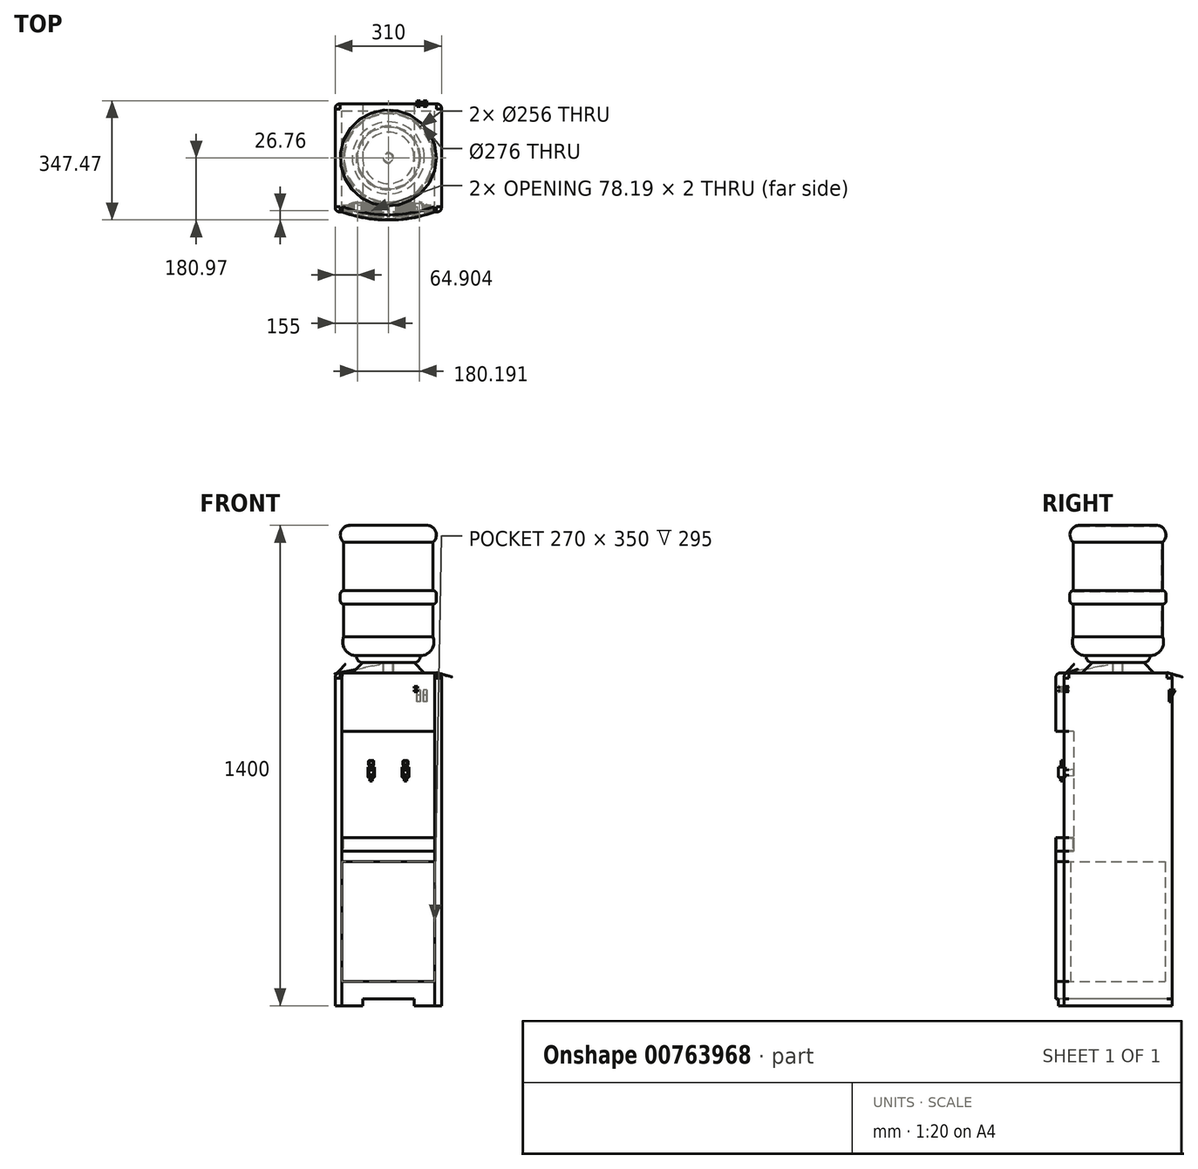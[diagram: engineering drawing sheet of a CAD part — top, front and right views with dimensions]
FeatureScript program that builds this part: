
annotation { "Feature Type Name" : "Feature", "Feature Type Description" : "" }
export const myFeature = defineFeature(function(context is Context, id is Id, definition is map)
    precondition{}
    {
        {
            var Q0;
            Q0=qCreatedBy(makeId("Top.planeOp"),FACE);
            var sketch = newSketch(context, id + "F0", { "sketchPlane" : qUnion([Q0])});
            skLineSegment(sketch, "E0.bottom", {"start": v(155, -157.5) * mm, "end": v(-155, -157.5) * mm});
            skLineSegment(sketch, "E0.top", {"start": v(155, 157.5) * mm, "end": v(-155, 157.5) * mm});
            skLineSegment(sketch, "E0.left", {"start": v(155, -157.5) * mm, "end": v(155, 157.5) * mm});
            skLineSegment(sketch, "E0.right", {"start": v(-155, -157.5) * mm, "end": v(-155, 157.5) * mm});
            skPoint(sketch, "E0.middle", {"position": v(0, 0) * mm});
            skArc(sketch, "E1", {"start": v(-135, -157.5) * mm, "mid": v(0, -180.97) * mm, "end": v(135, -157.5) * mm});
            skSolve(sketch);
        }
        {
            var Q0;
            Q0=makeQuery(id+"F0.imprint","IMPRINT",FACE,{"disambiguationData":[TD([[makeQuery(id+"F0.imprint","IMPRINT",EDGE,{"derivedFrom":sQuery(id+"F0.wireOp",EDGE,"E0.bottom")}),-1.0]])]});
            var Q1;
            {var subQ0=sQuery(id+"F0.wireOp",EDGE,"E1");Q1=makeQuery(id+"F0.imprint","IMPRINT",FACE,{"disambiguationData":[TD([[makeQuery(id+"F0.imprint","IMPRINT",EDGE,{"derivedFrom":subQ0}),1.0]])]});}
            extrude(context, id + "F1", {"entities" : qUnion([Q0, Q1]), "depth" : 970 * mm, "offsetDistance" : 25 * mm});
        }
        {
            var Q0;
            Q0=qCreatedBy(makeId("Front.planeOp"),FACE);
            var sketch = newSketch(context, id + "F2", { "sketchPlane" : qUnion([Q0])});
            skLineSegment(sketch, "E2.0", {"start": v(155, 970) * mm, "end": v(-155, 970) * mm});
            skLineSegment(sketch, "E3", {"start": v(105, 970) * mm, "end": v(75, 1000) * mm});
            skLineSegment(sketch, "E4", {"start": v(75, 1000) * mm, "end": v(0, 1000) * mm});
            skLineSegment(sketch, "E5", {"start": v(0, 1000) * mm, "end": v(0, 970) * mm});
            skLineSegment(sketch, "E6", {"start": v(15, 1000) * mm, "end": v(15, 970) * mm});
            skSolve(sketch);
        }
        {
            var Q0;
            {var subQ0=sQuery(id+"F2.wireOp",EDGE,"E3");Q0=makeQuery(id+"F2.imprint","IMPRINT",FACE,{"disambiguationData":[TD([[makeQuery(id+"F2.imprint","IMPRINT",EDGE,{"derivedFrom":subQ0}),1.0]])]});}
            var Q1;
            Q1=sQuery(id+"F2.wireOp",EDGE,"E5");
            revolve(context, id + "F3", {"operationType" : NewBodyOperationType.ADD, "surfaceOperationType" : NewSurfaceOperationType.NEW, "entities" : qUnion([Q0]), "axis" : qUnion([Q1]), "revolveType" : RevolveType.FULL});
        }
        {
            var Q0;
            Q0=qCreatedBy(makeId("Top.planeOp"),FACE);
            cPlane(context, id + "F4", {"entities" : qUnion([Q0]), "cplaneType" : CPlaneType.OFFSET, "offset" : 450 * mm, "width" : 150 * mm, "height" : 150 * mm});
        }
        {
            var Q0;
            Q0=qCreatedBy(id+"F4.planeOp",FACE);
            var sketch = newSketch(context, id + "F5", { "sketchPlane" : qUnion([Q0])});
            skArc(sketch, "E7.0.0", {"start": v(-135, -157.5) * mm, "mid": v(0, -180.97) * mm, "end": v(135, -157.5) * mm});
            skArc(sketch, "E7.0.2", {"start": v(135, -157.5) * mm, "mid": v(0, -180.97) * mm, "end": v(-135, -157.5) * mm});
            skLineSegment(sketch, "E8", {"start": v(-90, -129.3) * mm, "end": v(0, -129.3) * mm});
            skArc(sketch, "E9", {"start": v(-90, -129.3) * mm, "mid": v(-116.55, -136.93) * mm, "end": v(-135, -157.5) * mm});
            skLineSegment(sketch, "E10.MirrorCS", {"start": v(90, -129.3) * mm, "end": v(0, -129.3) * mm});
            skArc(sketch, "E11.MirrorCS", {"start": v(90, -129.3) * mm, "mid": v(116.55, -136.93) * mm, "end": v(135, -157.5) * mm});
            skSolve(sketch);
        }
        {
            var Q0;
            Q0 = qSketchRegion(id + "F5", true);
            extrude(context, id + "F6", {"entities" : qUnion([Q0]), "operationType" : NewBodyOperationType.REMOVE, "depth" : 350 * mm, "offsetDistance" : 25 * mm});
        }
        {
            var Q0;
            Q0=qCreatedBy(makeId("Front.planeOp"),FACE);
            var sketch = newSketch(context, id + "F7", { "sketchPlane" : qUnion([Q0])});
            skLineSegment(sketch, "E12.0", {"start": v(-135, 450) * mm, "end": v(-135, 0) * mm});
            skLineSegment(sketch, "E12.1", {"start": v(135, 450) * mm, "end": v(135, 0) * mm});
            skLineSegment(sketch, "E13", {"start": v(-135, 420) * mm, "end": v(135, 420) * mm});
            skLineSegment(sketch, "E14", {"start": v(-135, 70) * mm, "end": v(135, 70) * mm});
            skSolve(sketch);
        }
        {
            var Q0;
            Q0 = qSketchRegion(id + "F7", true);
            extrude(context, id + "F8", {"entities" : qUnion([Q0]), "operationType" : NewBodyOperationType.REMOVE, "endBound" : BoundingType.THROUGH_ALL, "depth" : 25 * mm, "offsetDistance" : 25 * mm, "hasSecondDirection" : true, "secondDirectionOppositeDirection" : true, "secondDirectionDepth" : (315 / 2 - 20) * mm});
        }
        {
            var Q0;
            Q0=qCreatedBy(makeId("Front.planeOp"),FACE);
            var sketch = newSketch(context, id + "F9", { "sketchPlane" : qUnion([Q0])});
            skLineSegment(sketch, "E15.bottom", {"start": v(-75, 20) * mm, "end": v(75, 20) * mm});
            skLineSegment(sketch, "E15.top", {"start": v(-75, 0) * mm, "end": v(75, 0) * mm});
            skLineSegment(sketch, "E15.left", {"start": v(-75, 20) * mm, "end": v(-75, 0) * mm});
            skLineSegment(sketch, "E15.right", {"start": v(75, 20) * mm, "end": v(75, 0) * mm});
            skSolve(sketch);
        }
        {
            var Q0;
            Q0 = qSketchRegion(id + "F9", true);
            extrude(context, id + "F10", {"entities" : qUnion([Q0]), "operationType" : NewBodyOperationType.REMOVE, "endBound" : BoundingType.THROUGH_ALL, "oppositeDirection" : true, "depth" : 25 * mm, "offsetDistance" : 25 * mm, "hasSecondDirection" : true, "secondDirectionBound" : SecondDirectionBoundingType.THROUGH_ALL, "secondDirectionOppositeDirection" : false, "secondDirectionDepth" : 25 * mm});
        }
        {
            var Q0;
            Q0=qCreatedBy(makeId("Front.planeOp"),FACE);
            var sketch = newSketch(context, id + "F11", { "sketchPlane" : qUnion([Q0])});
            skLineSegment(sketch, "E16.0", {"start": v(-15, 1000) * mm, "end": v(15, 1000) * mm});
            skLineSegment(sketch, "E17.0.0", {"start": v(-15, 970) * mm, "end": v(15, 970) * mm});
            skLineSegment(sketch, "E18", {"start": v(-15, 970) * mm, "end": v(-15, 1000) * mm});
            skLineSegment(sketch, "E19", {"start": v(0, 1400) * mm, "end": v(-112, 1400) * mm});
            skLineSegment(sketch, "E20", {"start": v(-130, 1350.55) * mm, "end": v(-130, 1210) * mm});
            skLineSegment(sketch, "E21", {"start": v(-130, 1170) * mm, "end": v(-130, 1075) * mm});
            skLineSegment(sketch, "E22.0", {"start": v(-75, 1000) * mm, "end": v(75, 1000) * mm});
            skArc(sketch, "E23", {"start": v(-92.88, 1020.1) * mm, "mid": v(-88.45, 1006.04) * mm, "end": v(-75, 1000) * mm});
            skLineSegment(sketch, "E24", {"start": v(-140, 1200) * mm, "end": v(-140, 1180) * mm});
            skArc(sketch, "E25", {"start": v(-140, 1180) * mm, "mid": v(-137.07, 1172.93) * mm, "end": v(-130, 1170) * mm});
            skLineSegment(sketch, "E26", {"start": v(-140, 1180) * mm, "end": v(-130, 1180) * mm, "construction": true});
            skLineSegment(sketch, "E27", {"start": v(-130, 1170) * mm, "end": v(-130, 1180) * mm, "construction": true});
            skArc(sketch, "E28", {"start": v(-112, 1400) * mm, "mid": v(-138.31, 1381.58) * mm, "end": v(-130, 1350.55) * mm});
            skArc(sketch, "E29", {"start": v(-130, 1210) * mm, "mid": v(-137.07, 1207.07) * mm, "end": v(-140, 1200) * mm});
            skLineSegment(sketch, "E30", {"start": v(-140, 1200) * mm, "end": v(-130, 1200) * mm, "construction": true});
            skLineSegment(sketch, "E31", {"start": v(-130, 1210) * mm, "end": v(-130, 1200) * mm, "construction": true});
            skArc(sketch, "E32", {"start": v(-130, 1075) * mm, "mid": v(-126.01, 1037.7) * mm, "end": v(-92.88, 1020.1) * mm});
            skLineSegment(sketch, "E33", {"start": v(-92.88, 1020.1) * mm, "end": v(0, 1020.1) * mm});
            skLineSegment(sketch, "E34", {"start": v(0, 1400) * mm, "end": v(0, 970) * mm});
            skLineSegment(sketch, "E35.0", {"start": v(-75, 1002) * mm, "end": v(75, 1002) * mm});
            skArc(sketch, "E35.1", {"start": v(-90.44, 1022.18) * mm, "mid": v(-87.7, 1008.28) * mm, "end": v(-75, 1002) * mm});
            skArc(sketch, "E35.2", {"start": v(-128, 1074.6) * mm, "mid": v(-123.77, 1037.98) * mm, "end": v(-90.44, 1022.18) * mm});
            skLineSegment(sketch, "E35.3", {"start": v(-128, 1172.25) * mm, "end": v(-128, 1074.6) * mm});
            skArc(sketch, "E35.4", {"start": v(-138, 1180) * mm, "mid": v(-134.9, 1173.68) * mm, "end": v(-128, 1172.25) * mm});
            skLineSegment(sketch, "E35.5", {"start": v(-138, 1200) * mm, "end": v(-138, 1180) * mm});
            skLineSegment(sketch, "E35.6", {"start": v(0, 1398) * mm, "end": v(-112, 1398) * mm});
            skArc(sketch, "E35.7", {"start": v(-112, 1398) * mm, "mid": v(-136.58, 1380.46) * mm, "end": v(-128, 1351.5) * mm});
            skLineSegment(sketch, "E35.8", {"start": v(-128, 1351.5) * mm, "end": v(-128, 1207.75) * mm});
            skArc(sketch, "E35.9", {"start": v(-128, 1207.75) * mm, "mid": v(-134.9, 1206.32) * mm, "end": v(-138, 1200) * mm});
            skLineSegment(sketch, "E36", {"start": v(-13, 970) * mm, "end": v(-13, 1002) * mm});
            skSolve(sketch);
        }
        {
            var Q0;
            {var subQ0=sQuery(id+"F11.wireOp",EDGE,"E18");Q0=makeQuery(id+"F11.imprint","IMPRINT",FACE,{"disambiguationData":[TD([[makeQuery(id+"F11.imprint","IMPRINT",EDGE,{"derivedFrom":subQ0}),-1.0]])]});}
            var Q1;
            {var subQ1=sQuery(id+"F11.wireOp",EDGE,"E23");Q1=makeQuery(id+"F11.imprint","IMPRINT",FACE,{"disambiguationData":[TD([[makeQuery(id+"F11.imprint","IMPRINT",EDGE,{"derivedFrom":subQ1}),1.0]])]});}
            var Q2;
            {var subQ1=sQuery(id+"F11.wireOp",EDGE,"E19");Q2=makeQuery(id+"F11.imprint","IMPRINT",FACE,{"disambiguationData":[TD([[makeQuery(id+"F11.imprint","IMPRINT",EDGE,{"derivedFrom":subQ1}),1.0]])]});}
            var Q3;
            Q3=sQuery(id+"F11.wireOp",EDGE,"E34");
            revolve(context, id + "F12", {"surfaceOperationType" : NewSurfaceOperationType.NEW, "entities" : qUnion([Q0, Q1, Q2]), "axis" : qUnion([Q3]), "revolveType" : RevolveType.FULL});
        }
        {
            var Q0;
            Q0=makeQuery(id+"F1.opExtrude","SWEPT_EDGE",EDGE,{"disambiguationData":[OSD([sQuery(id+"F0.wireOp",EDGE,"E0.top"),sQuery(id+"F0.wireOp",EDGE,"E0.right")])]});
            var Q1;
            Q1=makeQuery(id+"F1.opExtrude","SWEPT_EDGE",EDGE,{"disambiguationData":[OSD([sQuery(id+"F0.wireOp",EDGE,"E0.bottom"),sQuery(id+"F0.wireOp",EDGE,"E0.right")])]});
            var Q2;
            Q2=makeQuery(id+"F1.opExtrude","SWEPT_EDGE",EDGE,{"disambiguationData":[OSD([sQuery(id+"F0.wireOp",EDGE,"E0.bottom"),sQuery(id+"F0.wireOp",EDGE,"E0.left")])]});
            var Q3;
            Q3=makeQuery(id+"F1.opExtrude","SWEPT_EDGE",EDGE,{"disambiguationData":[OSD([sQuery(id+"F0.wireOp",EDGE,"E0.top"),sQuery(id+"F0.wireOp",EDGE,"E0.left")])]});
            var Q4;
            Q4=makeQuery(id+"F1.opExtrude","CAP_EDGE",EDGE,{"disambiguationData":[OSD([sQuery(id+"F0.wireOp",EDGE,"E0.top")])],"isStart":false});
            var Q5;
            Q5=makeQuery(id+"F1.opExtrude","CAP_EDGE",EDGE,{"disambiguationData":[OSD([sQuery(id+"F0.wireOp",EDGE,"E0.left")])],"isStart":false});
            var Q6;
            Q6=makeQuery(id+"F1.opExtrude","CAP_EDGE",EDGE,{"disambiguationData":[OSD([sQuery(id+"F0.wireOp",EDGE,"E0.right")])],"isStart":false});
            var Q7;
            Q7=makeQuery(id+"F1.opExtrude","CAP_EDGE",EDGE,{"disambiguationData":[OSD([sQuery(id+"F0.wireOp",EDGE,"E1")])],"isStart":false});
            var Q8;
            {var subQ0=sQuery(id+"F0.wireOp",EDGE,"E0.bottom");Q8=makeQuery(id+"F1.opExtrude","CAP_EDGE",EDGE,{"disambiguationData":[OSD([subQ0]),TDD([makeQuery(id+"F0.imprint","IMPRINT",EDGE,{"disambiguationData":[TD([[makeQuery(id+"F0.imprint","INTERSECT",VERTEX,{"derivedFrom":[subQ0,sQuery(id+"F0.wireOp",EDGE,"E0.right")]}),1.0]])],"derivedFrom":subQ0})])],"isStart":false});}
            var Q9;
            {var subQ0=sQuery(id+"F0.wireOp",EDGE,"E0.bottom");Q9=makeQuery(id+"F1.opExtrude","CAP_EDGE",EDGE,{"disambiguationData":[OSD([subQ0]),TDD([makeQuery(id+"F0.imprint","IMPRINT",EDGE,{"disambiguationData":[TD([[makeQuery(id+"F0.imprint","INTERSECT",VERTEX,{"derivedFrom":[subQ0,sQuery(id+"F0.wireOp",EDGE,"E0.left")]}),-1.0]])],"derivedFrom":subQ0})])],"isStart":false});}
            fillet(context, id + "F13", {"entities" : qUnion([Q0, Q1, Q2, Q3, Q4, Q5, Q6, Q7, Q8, Q9]), "radius" : 15 * mm, "tangentPropagation" : true, "crossSection" : FilletCrossSection.CURVATURE, "magnitude" : 0.5, "defaultsChanged" : false, "vertexSettings" : []});
        }
        {
            var Q0;
            Q0=makeQuery(id+"F6.boolean.opBoolean","COPY",FACE,{"derivedFrom":makeQuery(id+"F6.opExtrude","CAP_FACE",FACE,{"disambiguationData":[OSD([sQuery(id+"F5.wireOp",EDGE,"E7.0.2"),sQuery(id+"F5.wireOp",EDGE,"E8"),sQuery(id+"F5.wireOp",EDGE,"E9"),sQuery(id+"F5.wireOp",EDGE,"E10.MirrorCS"),sQuery(id+"F5.wireOp",EDGE,"E11.MirrorCS")])],"isStart":true})});
            var sketch = newSketch(context, id + "F14", { "sketchPlane" : qUnion([Q0])});
            skArc(sketch, "E37.0", {"start": v(-90, -129.3) * mm, "mid": v(-116.55, -136.93) * mm, "end": v(-135, -157.5) * mm});
            skLineSegment(sketch, "E37.1", {"start": v(90, -129.3) * mm, "end": v(-90, -129.3) * mm});
            skArc(sketch, "E37.2", {"start": v(90, -129.3) * mm, "mid": v(116.55, -136.93) * mm, "end": v(135, -157.5) * mm});
            skArc(sketch, "E37.3", {"start": v(135, -157.5) * mm, "mid": v(0, -180.97) * mm, "end": v(-135, -157.5) * mm});
            skSolve(sketch);
        }
        {
            var Q0;
            Q0=makeQuery(id+"F14.imprint","IMPRINT",FACE,{"disambiguationData":[TD([[makeQuery(id+"F14.imprint","IMPRINT",EDGE,{"derivedFrom":sQuery(id+"F14.wireOp",EDGE,"E37.0")}),1.0]])]});
            var Q1;
            Q1 = qConstructionFilter(qBodyType(qCreatedBy(id + "F14" ,EDGE), BodyType.WIRE), ConstructionObject.NO);
            extrude(context, id + "F15", {"entities" : qUnion([Q0]), "surfaceEntities" : qUnion([Q1]), "depth" : 40 * mm, "offsetDistance" : 25 * mm});
        }
        {
            var Q0;
            Q0=makeQuery(id+"F15.opExtrude","CAP_FACE",FACE,{"disambiguationData":[OSD([sQuery(id+"F14.wireOp",EDGE,"E37.0"),sQuery(id+"F14.wireOp",EDGE,"E37.1"),sQuery(id+"F14.wireOp",EDGE,"E37.2"),sQuery(id+"F14.wireOp",EDGE,"E37.3")])],"isStart":false});
            shell(context, id + "F16", {"entities" : qUnion([Q0]), "thickness" : 2 * mm});
        }
        {
            var Q0;
            Q0=makeQuery(id+"F15.opExtrude","CAP_FACE",FACE,{"disambiguationData":[OSD([sQuery(id+"F14.wireOp",EDGE,"E37.0"),sQuery(id+"F14.wireOp",EDGE,"E37.1"),sQuery(id+"F14.wireOp",EDGE,"E37.2"),sQuery(id+"F14.wireOp",EDGE,"E37.3")])],"isStart":false});
            var sketch = newSketch(context, id + "F17", { "sketchPlane" : qUnion([Q0])});
            skArc(sketch, "E38.0", {"start": v(-90, -131.3) * mm, "mid": v(-114.54, -138.04) * mm, "end": v(-132.18, -156.38) * mm});
            skLineSegment(sketch, "E38.1", {"start": v(90, -131.3) * mm, "end": v(-90, -131.3) * mm});
            skArc(sketch, "E38.2", {"start": v(132.18, -156.38) * mm, "mid": v(0, -178.97) * mm, "end": v(-132.18, -156.38) * mm});
            skArc(sketch, "E38.3", {"start": v(90, -131.3) * mm, "mid": v(114.54, -138.04) * mm, "end": v(132.18, -156.38) * mm});
            skLineSegment(sketch, "E39.0", {"start": v(90, -133.3) * mm, "end": v(-90, -133.3) * mm});
            skArc(sketch, "E39.1", {"start": v(90, -133.3) * mm, "mid": v(112.5, -139.17) * mm, "end": v(129.24, -155.29) * mm});
            skArc(sketch, "E39.2", {"start": v(129.24, -155.29) * mm, "mid": v(0, -176.97) * mm, "end": v(-129.24, -155.29) * mm});
            skArc(sketch, "E39.3", {"start": v(-90, -133.3) * mm, "mid": v(-112.5, -139.17) * mm, "end": v(-129.24, -155.29) * mm});
            skLineSegment(sketch, "E40", {"start": v(0, -112.71) * mm, "end": v(0, -215.15) * mm, "construction": true});
            skLineSegment(sketch, "E41", {"start": v(-50, -106.6) * mm, "end": v(-50, -205.9) * mm, "construction": true});
            skLineSegment(sketch, "E42.bottom", {"start": v(-57.5, -156.3) * mm, "end": v(-42.5, -156.3) * mm});
            skLineSegment(sketch, "E42.top", {"start": v(-57.5, -171.3) * mm, "end": v(-42.5, -171.3) * mm});
            skLineSegment(sketch, "E42.left", {"start": v(-57.5, -156.3) * mm, "end": v(-57.5, -171.3) * mm});
            skLineSegment(sketch, "E42.right", {"start": v(-42.5, -156.3) * mm, "end": v(-42.5, -171.3) * mm});
            skLineSegment(sketch, "E43", {"start": v(-51, -156.3) * mm, "end": v(-51, -133.3) * mm});
            skLineSegment(sketch, "E44.MirrorCS", {"start": v(-49, -156.3) * mm, "end": v(-49, -133.3) * mm});
            skLineSegment(sketch, "E45", {"start": v(-51, -171.3) * mm, "end": v(-51, -173.67) * mm});
            skLineSegment(sketch, "E46", {"start": v(-49, -171.3) * mm, "end": v(-49, -173.93) * mm});
            skLineSegment(sketch, "E47", {"start": v(-1, -133.3) * mm, "end": v(-1, -176.97) * mm});
            skLineSegment(sketch, "E48", {"start": v(1, -133.3) * mm, "end": v(1, -176.97) * mm});
            skLineSegment(sketch, "E49", {"start": v(-49, -135.21) * mm, "end": v(-1, -135.21) * mm});
            skLineSegment(sketch, "E50.0.1.0", {"start": v(-49, -137.21) * mm, "end": v(-1, -137.21) * mm});
            skLineSegment(sketch, "E50.0.2.0", {"start": v(-49, -139.21) * mm, "end": v(-1, -139.21) * mm});
            skLineSegment(sketch, "E50.0.3.0", {"start": v(-49, -141.21) * mm, "end": v(-1, -141.21) * mm});
            skLineSegment(sketch, "E50.0.4.0", {"start": v(-49, -143.21) * mm, "end": v(-1, -143.21) * mm});
            skLineSegment(sketch, "E50.0.5.0", {"start": v(-49, -145.21) * mm, "end": v(-1, -145.21) * mm});
            skLineSegment(sketch, "E50.0.6.0", {"start": v(-49, -147.21) * mm, "end": v(-1, -147.21) * mm});
            skLineSegment(sketch, "E50.0.7.0", {"start": v(-49, -149.21) * mm, "end": v(-1, -149.21) * mm});
            skLineSegment(sketch, "E50.0.8.0", {"start": v(-49, -151.21) * mm, "end": v(-1, -151.21) * mm});
            skLineSegment(sketch, "E50.0.9.0", {"start": v(-49, -153.21) * mm, "end": v(-1, -153.21) * mm});
            skLineSegment(sketch, "E50.0.10.0", {"start": v(-49, -155.21) * mm, "end": v(-1, -155.21) * mm});
            skLineSegment(sketch, "E50.0.11.0", {"start": v(-42.5, -157.21) * mm, "end": v(-1, -157.21) * mm});
            skLineSegment(sketch, "E50.0.12.0", {"start": v(-44.5, -159.21) * mm, "end": v(-1, -159.21) * mm});
            skLineSegment(sketch, "E50.0.13.0", {"start": v(-44.5, -161.21) * mm, "end": v(-1, -161.21) * mm});
            skLineSegment(sketch, "E50.0.14.0", {"start": v(-44.5, -163.21) * mm, "end": v(-1, -163.21) * mm});
            skLineSegment(sketch, "E50.0.15.0", {"start": v(-49, -165.21) * mm, "end": v(-1, -165.21) * mm});
            skLineSegment(sketch, "E50.0.16.0", {"start": v(-49, -167.21) * mm, "end": v(-1, -167.21) * mm});
            skLineSegment(sketch, "E50.0.17.0", {"start": v(-49, -169.21) * mm, "end": v(-1, -169.21) * mm});
            skLineSegment(sketch, "E50.0.18.0", {"start": v(-49, -171.21) * mm, "end": v(-1, -171.21) * mm});
            skLineSegment(sketch, "E50.0.19.0", {"start": v(-49, -173.21) * mm, "end": v(-1, -173.21) * mm});
            skLineSegment(sketch, "E50.0.20.0", {"start": v(-49, -175.21) * mm, "end": v(-1, -175.21) * mm});
            skLineSegment(sketch, "E50.direction1", {"start": v(-49, -135.21) * mm, "end": v(-24, -135.21) * mm, "construction": true});
            skLineSegment(sketch, "E50.direction2", {"start": v(-49, -135.21) * mm, "end": v(-49, -137.21) * mm, "construction": true});
            skLineSegment(sketch, "E51.MirrorCS", {"start": v(-51, -137.21) * mm, "end": v(-108.57, -137.21) * mm});
            skLineSegment(sketch, "E52.MirrorCS", {"start": v(-51, -139.21) * mm, "end": v(-112.57, -139.21) * mm});
            skLineSegment(sketch, "E53.MirrorCS", {"start": v(-51, -141.21) * mm, "end": v(-115.8, -141.21) * mm});
            skLineSegment(sketch, "E54.MirrorCS", {"start": v(-51, -143.21) * mm, "end": v(-118.53, -143.21) * mm});
            skLineSegment(sketch, "E55.MirrorCS", {"start": v(-51, -145.21) * mm, "end": v(-120.9, -145.21) * mm});
            skLineSegment(sketch, "E56.MirrorCS", {"start": v(-51, -147.21) * mm, "end": v(-122.96, -147.21) * mm});
            skLineSegment(sketch, "E57.MirrorCS", {"start": v(-51, -149.21) * mm, "end": v(-124.8, -149.21) * mm});
            skLineSegment(sketch, "E58.MirrorCS", {"start": v(-51, -151.21) * mm, "end": v(-126.43, -151.21) * mm});
            skLineSegment(sketch, "E59.MirrorCS", {"start": v(-51, -153.21) * mm, "end": v(-127.89, -153.21) * mm});
            skLineSegment(sketch, "E60.MirrorCS", {"start": v(-51, -155.21) * mm, "end": v(-129.2, -155.21) * mm});
            skLineSegment(sketch, "E61.MirrorCS", {"start": v(-57.5, -157.21) * mm, "end": v(-123.53, -157.21) * mm});
            skLineSegment(sketch, "E62.MirrorCS", {"start": v(-57.5, -159.21) * mm, "end": v(-117.26, -159.21) * mm});
            skLineSegment(sketch, "E63.MirrorCS", {"start": v(-57.5, -161.21) * mm, "end": v(-110.6, -161.21) * mm});
            skLineSegment(sketch, "E64.MirrorCS", {"start": v(-57.5, -163.21) * mm, "end": v(-103.48, -163.21) * mm});
            skLineSegment(sketch, "E65.MirrorCS", {"start": v(-49, -165.21) * mm, "end": v(-50, -165.21) * mm});
            skLineSegment(sketch, "E66.MirrorCS", {"start": v(-57.5, -167.21) * mm, "end": v(-99, -167.21) * mm});
            skLineSegment(sketch, "E67.MirrorCS", {"start": v(-57.5, -169.21) * mm, "end": v(-99, -169.21) * mm});
            skLineSegment(sketch, "E68.MirrorCS", {"start": v(-51, -171.21) * mm, "end": v(-99, -171.21) * mm});
            skLineSegment(sketch, "E69.MirrorCS", {"start": v(-51, -173.21) * mm, "end": v(-99, -173.21) * mm});
            skPoint(sketch, "E70.orphan", {"position": v(-99, -137.21) * mm});
            skPoint(sketch, "E71.orphan", {"position": v(-99, -139.21) * mm});
            skPoint(sketch, "E72.orphan", {"position": v(-99, -141.21) * mm});
            skPoint(sketch, "E73.orphan", {"position": v(-99, -143.21) * mm});
            skPoint(sketch, "E74.orphan", {"position": v(-99, -145.21) * mm});
            skPoint(sketch, "E75.orphan", {"position": v(-99, -147.21) * mm});
            skPoint(sketch, "E76.orphan", {"position": v(-99, -149.21) * mm});
            skPoint(sketch, "E77.orphan", {"position": v(-99, -151.21) * mm});
            skPoint(sketch, "E78.orphan", {"position": v(-99, -153.21) * mm});
            skPoint(sketch, "E79.orphan", {"position": v(-99, -155.21) * mm});
            skPoint(sketch, "E80.orphan", {"position": v(-99, -157.21) * mm});
            skPoint(sketch, "E81.orphan", {"position": v(-99, -159.21) * mm});
            skPoint(sketch, "E82.orphan", {"position": v(-99, -161.21) * mm});
            skPoint(sketch, "E83.orphan", {"position": v(-99, -163.21) * mm});
            skLineSegment(sketch, "E84", {"start": v(-51, -135.21) * mm, "end": v(-103.14, -135.21) * mm});
            skLineSegment(sketch, "E85.0", {"start": v(-55.5, -158.3) * mm, "end": v(-44.5, -158.3) * mm});
            skLineSegment(sketch, "E85.1", {"start": v(-55.5, -158.3) * mm, "end": v(-55.5, -169.3) * mm});
            skLineSegment(sketch, "E85.2", {"start": v(-55.5, -169.3) * mm, "end": v(-44.5, -169.3) * mm});
            skLineSegment(sketch, "E85.3", {"start": v(-44.5, -158.3) * mm, "end": v(-44.5, -169.3) * mm});
            skPoint(sketch, "E86.orphan", {"position": v(-51, -157.21) * mm});
            skPoint(sketch, "E87.orphan", {"position": v(-51, -161.21) * mm});
            skPoint(sketch, "E88.orphan", {"position": v(-51, -165.21) * mm});
            skPoint(sketch, "E89.orphan", {"position": v(-51, -159.21) * mm});
            skPoint(sketch, "E90.orphan", {"position": v(-51, -163.21) * mm});
            skLineSegment(sketch, "E91.trimOffspring", {"start": v(-57.5, -165.21) * mm, "end": v(-99, -165.21) * mm});
            skPoint(sketch, "E92.orphan", {"position": v(-51, -167.21) * mm});
            skPoint(sketch, "E93.orphan", {"position": v(-51, -169.21) * mm});
            skPoint(sketch, "E94.orphan", {"position": v(-49, -159.21) * mm});
            skPoint(sketch, "E95.orphan", {"position": v(-49, -157.21) * mm});
            skPoint(sketch, "E96.orphan", {"position": v(-49, -161.21) * mm});
            skPoint(sketch, "E97.orphan", {"position": v(-49, -163.21) * mm});
            skLineSegment(sketch, "E98.MirrorCS", {"start": v(49, -165.21) * mm, "end": v(1, -165.21) * mm});
            skLineSegment(sketch, "E99.MirrorCS", {"start": v(44.5, -163.21) * mm, "end": v(1, -163.21) * mm});
            skLineSegment(sketch, "E100.MirrorCS", {"start": v(49, -167.21) * mm, "end": v(1, -167.21) * mm});
            skLineSegment(sketch, "E101.MirrorCS", {"start": v(44.5, -159.21) * mm, "end": v(1, -159.21) * mm});
            skLineSegment(sketch, "E102.MirrorCS", {"start": v(49, -171.21) * mm, "end": v(1, -171.21) * mm});
            skLineSegment(sketch, "E103.MirrorCS", {"start": v(42.5, -157.21) * mm, "end": v(1, -157.21) * mm});
            skLineSegment(sketch, "E104.MirrorCS", {"start": v(49, -175.21) * mm, "end": v(1, -175.21) * mm});
            skLineSegment(sketch, "E105.MirrorCS", {"start": v(49, -173.21) * mm, "end": v(1, -173.21) * mm});
            skLineSegment(sketch, "E106.MirrorCS", {"start": v(44.5, -161.21) * mm, "end": v(1, -161.21) * mm});
            skLineSegment(sketch, "E107.MirrorCS", {"start": v(49, -169.21) * mm, "end": v(1, -169.21) * mm});
            skLineSegment(sketch, "E108.MirrorCS", {"start": v(49, -135.21) * mm, "end": v(1, -135.21) * mm});
            skLineSegment(sketch, "E109.MirrorCS", {"start": v(49, -145.21) * mm, "end": v(1, -145.21) * mm});
            skLineSegment(sketch, "E110.MirrorCS", {"start": v(49, -137.21) * mm, "end": v(1, -137.21) * mm});
            skLineSegment(sketch, "E111.MirrorCS", {"start": v(49, -143.21) * mm, "end": v(1, -143.21) * mm});
            skLineSegment(sketch, "E112.MirrorCS", {"start": v(49, -153.21) * mm, "end": v(1, -153.21) * mm});
            skLineSegment(sketch, "E113.MirrorCS", {"start": v(49, -141.21) * mm, "end": v(1, -141.21) * mm});
            skLineSegment(sketch, "E114.MirrorCS", {"start": v(49, -151.21) * mm, "end": v(1, -151.21) * mm});
            skLineSegment(sketch, "E115.MirrorCS", {"start": v(49, -149.21) * mm, "end": v(1, -149.21) * mm});
            skLineSegment(sketch, "E116.MirrorCS", {"start": v(49, -147.21) * mm, "end": v(1, -147.21) * mm});
            skLineSegment(sketch, "E117.MirrorCS", {"start": v(49, -139.21) * mm, "end": v(1, -139.21) * mm});
            skLineSegment(sketch, "E118.MirrorCS", {"start": v(49, -155.21) * mm, "end": v(1, -155.21) * mm});
            skLineSegment(sketch, "E119.MirrorCS", {"start": v(42.5, -156.3) * mm, "end": v(42.5, -171.3) * mm});
            skLineSegment(sketch, "E120.MirrorCS", {"start": v(44.5, -158.3) * mm, "end": v(44.5, -169.3) * mm});
            skLineSegment(sketch, "E121.MirrorCS", {"start": v(55.5, -158.3) * mm, "end": v(55.5, -169.3) * mm});
            skLineSegment(sketch, "E122.MirrorCS", {"start": v(57.5, -156.3) * mm, "end": v(42.5, -156.3) * mm});
            skLineSegment(sketch, "E123.MirrorCS", {"start": v(51, -171.21) * mm, "end": v(99, -171.21) * mm});
            skLineSegment(sketch, "E124.MirrorCS", {"start": v(57.5, -156.3) * mm, "end": v(57.5, -171.3) * mm});
            skLineSegment(sketch, "E125.MirrorCS", {"start": v(57.5, -171.3) * mm, "end": v(42.5, -171.3) * mm});
            skLineSegment(sketch, "E126.MirrorCS", {"start": v(49, -171.3) * mm, "end": v(49, -173.93) * mm});
            skLineSegment(sketch, "E127.MirrorCS", {"start": v(51, -171.3) * mm, "end": v(51, -173.67) * mm});
            skLineSegment(sketch, "E128.MirrorCS", {"start": v(51, -151.21) * mm, "end": v(126.43, -151.21) * mm});
            skLineSegment(sketch, "E129.MirrorCS", {"start": v(51, -155.21) * mm, "end": v(129.2, -155.21) * mm});
            skLineSegment(sketch, "E130.MirrorCS", {"start": v(57.5, -165.21) * mm, "end": v(99, -165.21) * mm});
            skLineSegment(sketch, "E131.MirrorCS", {"start": v(57.5, -157.21) * mm, "end": v(123.53, -157.21) * mm});
            skLineSegment(sketch, "E132.MirrorCS", {"start": v(51, -153.21) * mm, "end": v(127.89, -153.21) * mm});
            skLineSegment(sketch, "E133.MirrorCS", {"start": v(57.5, -159.21) * mm, "end": v(117.26, -159.21) * mm});
            skLineSegment(sketch, "E134.MirrorCS", {"start": v(57.5, -167.21) * mm, "end": v(99, -167.21) * mm});
            skLineSegment(sketch, "E135.MirrorCS", {"start": v(51, -141.21) * mm, "end": v(115.8, -141.21) * mm});
            skLineSegment(sketch, "E136.MirrorCS", {"start": v(51, -149.21) * mm, "end": v(124.8, -149.21) * mm});
            skLineSegment(sketch, "E137.MirrorCS", {"start": v(51, -147.21) * mm, "end": v(122.96, -147.21) * mm});
            skLineSegment(sketch, "E138.MirrorCS", {"start": v(51, -137.21) * mm, "end": v(108.57, -137.21) * mm});
            skLineSegment(sketch, "E139.MirrorCS", {"start": v(57.5, -169.21) * mm, "end": v(99, -169.21) * mm});
            skLineSegment(sketch, "E140.MirrorCS", {"start": v(51, -145.21) * mm, "end": v(120.9, -145.21) * mm});
            skLineSegment(sketch, "E141.MirrorCS", {"start": v(51, -139.21) * mm, "end": v(112.57, -139.21) * mm});
            skLineSegment(sketch, "E142.MirrorCS", {"start": v(51, -135.21) * mm, "end": v(103.14, -135.21) * mm});
            skLineSegment(sketch, "E143.MirrorCS", {"start": v(-90, -133.3) * mm, "end": v(90, -133.3) * mm});
            skLineSegment(sketch, "E144.MirrorCS", {"start": v(51, -143.21) * mm, "end": v(118.53, -143.21) * mm});
            skLineSegment(sketch, "E145.MirrorCS", {"start": v(57.5, -163.21) * mm, "end": v(103.48, -163.21) * mm});
            skLineSegment(sketch, "E146.MirrorCS", {"start": v(57.5, -161.21) * mm, "end": v(110.6, -161.21) * mm});
            skPoint(sketch, "E147.MirrorP", {"position": v(99, -145.21) * mm});
            skPoint(sketch, "E148.MirrorP", {"position": v(99, -141.21) * mm});
            skPoint(sketch, "E149.MirrorP", {"position": v(99, -143.21) * mm});
            skPoint(sketch, "E150.MirrorP", {"position": v(99, -139.21) * mm});
            skPoint(sketch, "E151.MirrorP", {"position": v(99, -137.21) * mm});
            skPoint(sketch, "E152.MirrorP", {"position": v(99, -155.21) * mm});
            skPoint(sketch, "E153.MirrorP", {"position": v(99, -147.21) * mm});
            skPoint(sketch, "E154.MirrorP", {"position": v(99, -149.21) * mm});
            skPoint(sketch, "E155.MirrorP", {"position": v(99, -157.21) * mm});
            skPoint(sketch, "E156.MirrorP", {"position": v(99, -151.21) * mm});
            skPoint(sketch, "E157.MirrorP", {"position": v(99, -153.21) * mm});
            skLineSegment(sketch, "E158.MirrorCS", {"start": v(55.5, -158.3) * mm, "end": v(44.5, -158.3) * mm});
            skLineSegment(sketch, "E159.MirrorCS", {"start": v(55.5, -169.3) * mm, "end": v(44.5, -169.3) * mm});
            skLineSegment(sketch, "E160.MirrorCS", {"start": v(51, -156.3) * mm, "end": v(51, -133.3) * mm});
            skLineSegment(sketch, "E161.MirrorCS", {"start": v(49, -156.3) * mm, "end": v(49, -133.3) * mm});
            skLineSegment(sketch, "E162.MirrorCS", {"start": v(51, -173.21) * mm, "end": v(99, -173.21) * mm});
            skSolve(sketch);
        }
        {
            var Q0;
            {var subQ16=sQuery(id+"F17.wireOp",EDGE,"E38.0");Q0=makeQuery(id+"F17.imprint","IMPRINT",FACE,{"disambiguationData":[TD([[makeQuery(id+"F17.imprint","IMPRINT",EDGE,{"derivedFrom":subQ16}),1.0]])]});}
            var Q1;
            {var subQ0=sQuery(id+"F17.wireOp",EDGE,"E66.MirrorCS");var subQ1=sQuery(id+"F17.wireOp",EDGE,"E38.2");var subQ2=makeQuery(id+"F17.imprint","INTERSECT",VERTEX,{"derivedFrom":[subQ1,subQ0]});Q1=makeQuery(id+"F17.imprint","IMPRINT",FACE,{"disambiguationData":[TD([[makeQuery(id+"F17.imprint","IMPRINT",EDGE,{"disambiguationData":[TD([[subQ2,1.0]])],"derivedFrom":subQ1}),-1.0]])]});}
            var Q2;
            {var subQ0=sQuery(id+"F17.wireOp",EDGE,"E67.MirrorCS");var subQ1=sQuery(id+"F17.wireOp",EDGE,"E38.2");var subQ2=makeQuery(id+"F17.imprint","INTERSECT",VERTEX,{"derivedFrom":[subQ1,subQ0]});Q2=makeQuery(id+"F17.imprint","IMPRINT",FACE,{"disambiguationData":[TD([[makeQuery(id+"F17.imprint","IMPRINT",EDGE,{"disambiguationData":[TD([[subQ2,1.0]])],"derivedFrom":subQ1}),-1.0]])]});}
            var Q3;
            {var subQ0=sQuery(id+"F17.wireOp",EDGE,"E68.MirrorCS");var subQ1=sQuery(id+"F17.wireOp",EDGE,"E38.2");var subQ2=makeQuery(id+"F17.imprint","INTERSECT",VERTEX,{"derivedFrom":[subQ1,subQ0]});Q3=makeQuery(id+"F17.imprint","IMPRINT",FACE,{"disambiguationData":[TD([[makeQuery(id+"F17.imprint","IMPRINT",EDGE,{"disambiguationData":[TD([[subQ2,1.0]])],"derivedFrom":subQ1}),-1.0]])]});}
            var Q4;
            {var subQ0=sQuery(id+"F17.wireOp",EDGE,"E134.MirrorCS");var subQ1=sQuery(id+"F17.wireOp",EDGE,"E38.2");var subQ2=makeQuery(id+"F17.imprint","INTERSECT",VERTEX,{"derivedFrom":[subQ1,subQ0]});Q4=makeQuery(id+"F17.imprint","IMPRINT",FACE,{"disambiguationData":[TD([[makeQuery(id+"F17.imprint","IMPRINT",EDGE,{"disambiguationData":[TD([[subQ2,-1.0]])],"derivedFrom":subQ1}),-1.0]])]});}
            var Q5;
            {var subQ0=sQuery(id+"F17.wireOp",EDGE,"E123.MirrorCS");var subQ1=sQuery(id+"F17.wireOp",EDGE,"E38.2");var subQ2=makeQuery(id+"F17.imprint","INTERSECT",VERTEX,{"derivedFrom":[subQ1,subQ0]});Q5=makeQuery(id+"F17.imprint","IMPRINT",FACE,{"disambiguationData":[TD([[makeQuery(id+"F17.imprint","IMPRINT",EDGE,{"disambiguationData":[TD([[subQ2,1.0]])],"derivedFrom":subQ1}),-1.0]])]});}
            var Q6;
            {var subQ7=sQuery(id+"F17.wireOp",EDGE,"E69.MirrorCS");var subQ9=sQuery(id+"F17.wireOp",EDGE,"E38.2");var subQ10=makeQuery(id+"F17.imprint","INTERSECT",VERTEX,{"derivedFrom":[subQ9,subQ7]});Q6=makeQuery(id+"F17.imprint","IMPRINT",FACE,{"disambiguationData":[TD([[makeQuery(id+"F17.imprint","IMPRINT",EDGE,{"disambiguationData":[TD([[subQ10,1.0]])],"derivedFrom":subQ9}),-1.0]])]});}
            var Q7;
            {var subQ0=sQuery(id+"F17.wireOp",EDGE,"E162.MirrorCS");var subQ1=sQuery(id+"F17.wireOp",EDGE,"E38.2");var subQ2=makeQuery(id+"F17.imprint","INTERSECT",VERTEX,{"derivedFrom":[subQ1,subQ0]});Q7=makeQuery(id+"F17.imprint","IMPRINT",FACE,{"disambiguationData":[TD([[makeQuery(id+"F17.imprint","IMPRINT",EDGE,{"disambiguationData":[TD([[subQ2,1.0]])],"derivedFrom":subQ1}),-1.0]])]});}
            extrude(context, id + "F18", {"entities" : qUnion([Q0, Q1, Q2, Q3, Q4, Q5, Q6, Q7]), "oppositeDirection" : true, "depth" : 2 * mm, "offsetDistance" : 25 * mm});
        }
        {
            var Q0;
            {var subQ0=sQuery(id+"F17.wireOp",EDGE,"E47");var subQ7=sQuery(id+"F17.wireOp",EDGE,"E39.2");var subQ8=makeQuery(id+"F17.imprint","INTERSECT",VERTEX,{"derivedFrom":[subQ7,subQ0]});Q0=makeQuery(id+"F17.imprint","IMPRINT",FACE,{"disambiguationData":[TD([[makeQuery(id+"F17.imprint","IMPRINT",EDGE,{"disambiguationData":[TD([[subQ8,1.0]])],"derivedFrom":subQ7}),-1.0]])]});}
            var Q1;
            {var subQ0=sQuery(id+"F17.wireOp",EDGE,"E49");Q1=makeQuery(id+"F17.imprint","IMPRINT",FACE,{"disambiguationData":[TD([[makeQuery(id+"F17.imprint","IMPRINT",EDGE,{"derivedFrom":subQ0}),-1.0]])]});}
            var Q2;
            {var subQ0=sQuery(id+"F17.wireOp",EDGE,"E50.0.2.0");Q2=makeQuery(id+"F17.imprint","IMPRINT",FACE,{"disambiguationData":[TD([[makeQuery(id+"F17.imprint","IMPRINT",EDGE,{"derivedFrom":subQ0}),-1.0]])]});}
            var Q3;
            {var subQ0=sQuery(id+"F17.wireOp",EDGE,"E50.0.4.0");Q3=makeQuery(id+"F17.imprint","IMPRINT",FACE,{"disambiguationData":[TD([[makeQuery(id+"F17.imprint","IMPRINT",EDGE,{"derivedFrom":subQ0}),-1.0]])]});}
            var Q4;
            {var subQ0=sQuery(id+"F17.wireOp",EDGE,"E50.0.6.0");Q4=makeQuery(id+"F17.imprint","IMPRINT",FACE,{"disambiguationData":[TD([[makeQuery(id+"F17.imprint","IMPRINT",EDGE,{"derivedFrom":subQ0}),-1.0]])]});}
            var Q5;
            {var subQ0=sQuery(id+"F17.wireOp",EDGE,"E50.0.8.0");Q5=makeQuery(id+"F17.imprint","IMPRINT",FACE,{"disambiguationData":[TD([[makeQuery(id+"F17.imprint","IMPRINT",EDGE,{"derivedFrom":subQ0}),-1.0]])]});}
            var Q6;
            {var subQ0=sQuery(id+"F17.wireOp",EDGE,"E50.0.10.0");Q6=makeQuery(id+"F17.imprint","IMPRINT",FACE,{"disambiguationData":[TD([[makeQuery(id+"F17.imprint","IMPRINT",EDGE,{"derivedFrom":subQ0}),-1.0]])]});}
            var Q7;
            {var subQ0=sQuery(id+"F17.wireOp",EDGE,"E50.0.12.0");var subQ1=sQuery(id+"F17.wireOp",EDGE,"E42.right");var subQ2=makeQuery(id+"F17.imprint","INTERSECT",VERTEX,{"derivedFrom":[subQ1,subQ0]});Q7=makeQuery(id+"F17.imprint","IMPRINT",FACE,{"disambiguationData":[TD([[makeQuery(id+"F17.imprint","IMPRINT",EDGE,{"disambiguationData":[TD([[subQ2,-1.0]])],"derivedFrom":subQ1}),1.0]])]});}
            var Q8;
            {var subQ0=sQuery(id+"F17.wireOp",EDGE,"E50.0.14.0");var subQ1=sQuery(id+"F17.wireOp",EDGE,"E42.right");var subQ2=makeQuery(id+"F17.imprint","INTERSECT",VERTEX,{"derivedFrom":[subQ1,subQ0]});Q8=makeQuery(id+"F17.imprint","IMPRINT",FACE,{"disambiguationData":[TD([[makeQuery(id+"F17.imprint","IMPRINT",EDGE,{"disambiguationData":[TD([[subQ2,-1.0]])],"derivedFrom":subQ1}),1.0]])]});}
            var Q9;
            {var subQ0=sQuery(id+"F17.wireOp",EDGE,"E50.0.16.0");var subQ1=sQuery(id+"F17.wireOp",EDGE,"E42.right");var subQ2=makeQuery(id+"F17.imprint","INTERSECT",VERTEX,{"derivedFrom":[subQ1,subQ0]});Q9=makeQuery(id+"F17.imprint","IMPRINT",FACE,{"disambiguationData":[TD([[makeQuery(id+"F17.imprint","IMPRINT",EDGE,{"disambiguationData":[TD([[subQ2,-1.0]])],"derivedFrom":subQ1}),1.0]])]});}
            var Q10;
            {var subQ3=sQuery(id+"F17.wireOp",EDGE,"E50.0.19.0");Q10=makeQuery(id+"F17.imprint","IMPRINT",FACE,{"disambiguationData":[TD([[makeQuery(id+"F17.imprint","IMPRINT",EDGE,{"derivedFrom":subQ3}),1.0]])]});}
            var Q11;
            {var subQ0=sQuery(id+"F17.wireOp",EDGE,"E47");var subQ1=sQuery(id+"F17.wireOp",EDGE,"E39.2");var subQ2=makeQuery(id+"F17.imprint","INTERSECT",VERTEX,{"derivedFrom":[subQ1,subQ0]});Q11=makeQuery(id+"F17.imprint","IMPRINT",FACE,{"disambiguationData":[TD([[makeQuery(id+"F17.imprint","IMPRINT",EDGE,{"disambiguationData":[TD([[subQ2,-1.0]])],"derivedFrom":subQ1}),-1.0]])]});}
            var Q12;
            {var subQ17=sQuery(id+"F17.wireOp",EDGE,"E85.0");Q12=makeQuery(id+"F17.imprint","IMPRINT",FACE,{"disambiguationData":[TD([[makeQuery(id+"F17.imprint","IMPRINT",EDGE,{"derivedFrom":subQ17}),1.0]])]});}
            var Q13;
            {var subQ0=sQuery(id+"F17.wireOp",EDGE,"E50.0.12.0");var subQ1=sQuery(id+"F17.wireOp",EDGE,"E42.right");var subQ2=makeQuery(id+"F17.imprint","INTERSECT",VERTEX,{"derivedFrom":[subQ1,subQ0]});Q13=makeQuery(id+"F17.imprint","IMPRINT",FACE,{"disambiguationData":[TD([[makeQuery(id+"F17.imprint","IMPRINT",EDGE,{"disambiguationData":[TD([[subQ2,-1.0]])],"derivedFrom":subQ1}),-1.0]])]});}
            var Q14;
            {var subQ0=sQuery(id+"F17.wireOp",EDGE,"E50.0.13.0");var subQ1=sQuery(id+"F17.wireOp",EDGE,"E42.right");var subQ2=makeQuery(id+"F17.imprint","INTERSECT",VERTEX,{"derivedFrom":[subQ1,subQ0]});Q14=makeQuery(id+"F17.imprint","IMPRINT",FACE,{"disambiguationData":[TD([[makeQuery(id+"F17.imprint","IMPRINT",EDGE,{"disambiguationData":[TD([[subQ2,-1.0]])],"derivedFrom":subQ1}),-1.0]])]});}
            var Q15;
            {var subQ0=sQuery(id+"F17.wireOp",EDGE,"E50.0.14.0");var subQ1=sQuery(id+"F17.wireOp",EDGE,"E42.right");var subQ2=makeQuery(id+"F17.imprint","INTERSECT",VERTEX,{"derivedFrom":[subQ1,subQ0]});Q15=makeQuery(id+"F17.imprint","IMPRINT",FACE,{"disambiguationData":[TD([[makeQuery(id+"F17.imprint","IMPRINT",EDGE,{"disambiguationData":[TD([[subQ2,-1.0]])],"derivedFrom":subQ1}),-1.0]])]});}
            var Q16;
            {var subQ0=sQuery(id+"F17.wireOp",EDGE,"E50.0.15.0");var subQ1=sQuery(id+"F17.wireOp",EDGE,"E42.right");var subQ2=makeQuery(id+"F17.imprint","INTERSECT",VERTEX,{"derivedFrom":[subQ1,subQ0]});Q16=makeQuery(id+"F17.imprint","IMPRINT",FACE,{"disambiguationData":[TD([[makeQuery(id+"F17.imprint","IMPRINT",EDGE,{"disambiguationData":[TD([[subQ2,-1.0]])],"derivedFrom":subQ1}),-1.0]])]});}
            var Q17;
            {var subQ0=sQuery(id+"F17.wireOp",EDGE,"E50.0.16.0");var subQ1=sQuery(id+"F17.wireOp",EDGE,"E42.right");var subQ2=makeQuery(id+"F17.imprint","INTERSECT",VERTEX,{"derivedFrom":[subQ1,subQ0]});Q17=makeQuery(id+"F17.imprint","IMPRINT",FACE,{"disambiguationData":[TD([[makeQuery(id+"F17.imprint","IMPRINT",EDGE,{"disambiguationData":[TD([[subQ2,-1.0]])],"derivedFrom":subQ1}),-1.0]])]});}
            var Q18;
            {var subQ10=sQuery(id+"F17.wireOp",EDGE,"E42.bottom");var subQ13=sQuery(id+"F17.wireOp",EDGE,"E43");var subQ21=makeQuery(id+"F17.imprint","INTERSECT",VERTEX,{"derivedFrom":[subQ10,subQ13]});Q18=makeQuery(id+"F17.imprint","IMPRINT",FACE,{"disambiguationData":[TD([[makeQuery(id+"F17.imprint","IMPRINT",EDGE,{"disambiguationData":[TD([[subQ21,-1.0]])],"derivedFrom":subQ10}),1.0]])]});}
            var Q19;
            {var subQ0=sQuery(id+"F17.wireOp",EDGE,"E45");var subQ6=sQuery(id+"F17.wireOp",EDGE,"E39.2");var subQ7=makeQuery(id+"F17.imprint","INTERSECT",VERTEX,{"derivedFrom":[subQ6,subQ0]});Q19=makeQuery(id+"F17.imprint","IMPRINT",FACE,{"disambiguationData":[TD([[makeQuery(id+"F17.imprint","IMPRINT",EDGE,{"disambiguationData":[TD([[subQ7,1.0]])],"derivedFrom":subQ6}),-1.0]])]});}
            var Q20;
            {var subQ3=sQuery(id+"F17.wireOp",EDGE,"E69.MirrorCS");var subQ9=sQuery(id+"F17.wireOp",EDGE,"E39.2");var subQ10=makeQuery(id+"F17.imprint","INTERSECT",VERTEX,{"derivedFrom":[subQ9,subQ3]});Q20=makeQuery(id+"F17.imprint","IMPRINT",FACE,{"disambiguationData":[TD([[makeQuery(id+"F17.imprint","IMPRINT",EDGE,{"disambiguationData":[TD([[subQ10,-1.0]])],"derivedFrom":subQ9}),-1.0]])]});}
            var Q21;
            {var subQ0=sQuery(id+"F17.wireOp",EDGE,"E67.MirrorCS");var subQ1=sQuery(id+"F17.wireOp",EDGE,"E39.2");var subQ2=makeQuery(id+"F17.imprint","INTERSECT",VERTEX,{"derivedFrom":[subQ1,subQ0]});Q21=makeQuery(id+"F17.imprint","IMPRINT",FACE,{"disambiguationData":[TD([[makeQuery(id+"F17.imprint","IMPRINT",EDGE,{"disambiguationData":[TD([[subQ2,-1.0]])],"derivedFrom":subQ1}),-1.0]])]});}
            var Q22;
            {var subQ0=sQuery(id+"F17.wireOp",EDGE,"E64.MirrorCS");Q22=makeQuery(id+"F17.imprint","IMPRINT",FACE,{"disambiguationData":[TD([[makeQuery(id+"F17.imprint","IMPRINT",EDGE,{"derivedFrom":subQ0}),1.0]])]});}
            var Q23;
            {var subQ0=sQuery(id+"F17.wireOp",EDGE,"E62.MirrorCS");Q23=makeQuery(id+"F17.imprint","IMPRINT",FACE,{"disambiguationData":[TD([[makeQuery(id+"F17.imprint","IMPRINT",EDGE,{"derivedFrom":subQ0}),1.0]])]});}
            var Q24;
            {var subQ6=sQuery(id+"F17.wireOp",EDGE,"E60.MirrorCS");Q24=makeQuery(id+"F17.imprint","IMPRINT",FACE,{"disambiguationData":[TD([[makeQuery(id+"F17.imprint","IMPRINT",EDGE,{"derivedFrom":subQ6}),1.0]])]});}
            var Q25;
            {var subQ0=sQuery(id+"F17.wireOp",EDGE,"E58.MirrorCS");Q25=makeQuery(id+"F17.imprint","IMPRINT",FACE,{"disambiguationData":[TD([[makeQuery(id+"F17.imprint","IMPRINT",EDGE,{"derivedFrom":subQ0}),1.0]])]});}
            var Q26;
            {var subQ0=sQuery(id+"F17.wireOp",EDGE,"E56.MirrorCS");Q26=makeQuery(id+"F17.imprint","IMPRINT",FACE,{"disambiguationData":[TD([[makeQuery(id+"F17.imprint","IMPRINT",EDGE,{"derivedFrom":subQ0}),1.0]])]});}
            var Q27;
            {var subQ0=sQuery(id+"F17.wireOp",EDGE,"E54.MirrorCS");Q27=makeQuery(id+"F17.imprint","IMPRINT",FACE,{"disambiguationData":[TD([[makeQuery(id+"F17.imprint","IMPRINT",EDGE,{"derivedFrom":subQ0}),1.0]])]});}
            var Q28;
            {var subQ0=sQuery(id+"F17.wireOp",EDGE,"E52.MirrorCS");Q28=makeQuery(id+"F17.imprint","IMPRINT",FACE,{"disambiguationData":[TD([[makeQuery(id+"F17.imprint","IMPRINT",EDGE,{"derivedFrom":subQ0}),1.0]])]});}
            var Q29;
            {var subQ0=sQuery(id+"F17.wireOp",EDGE,"E51.MirrorCS");Q29=makeQuery(id+"F17.imprint","IMPRINT",FACE,{"disambiguationData":[TD([[makeQuery(id+"F17.imprint","IMPRINT",EDGE,{"derivedFrom":subQ0}),-1.0]])]});}
            var Q30;
            {var subQ0=sQuery(id+"F17.wireOp",EDGE,"E108.MirrorCS");Q30=makeQuery(id+"F17.imprint","IMPRINT",FACE,{"disambiguationData":[TD([[makeQuery(id+"F17.imprint","IMPRINT",EDGE,{"derivedFrom":subQ0}),1.0]])]});}
            var Q31;
            {var subQ0=sQuery(id+"F17.wireOp",EDGE,"E113.MirrorCS");Q31=makeQuery(id+"F17.imprint","IMPRINT",FACE,{"disambiguationData":[TD([[makeQuery(id+"F17.imprint","IMPRINT",EDGE,{"derivedFrom":subQ0}),-1.0]])]});}
            var Q32;
            {var subQ0=sQuery(id+"F17.wireOp",EDGE,"E109.MirrorCS");Q32=makeQuery(id+"F17.imprint","IMPRINT",FACE,{"disambiguationData":[TD([[makeQuery(id+"F17.imprint","IMPRINT",EDGE,{"derivedFrom":subQ0}),-1.0]])]});}
            var Q33;
            {var subQ0=sQuery(id+"F17.wireOp",EDGE,"E115.MirrorCS");Q33=makeQuery(id+"F17.imprint","IMPRINT",FACE,{"disambiguationData":[TD([[makeQuery(id+"F17.imprint","IMPRINT",EDGE,{"derivedFrom":subQ0}),-1.0]])]});}
            var Q34;
            {var subQ0=sQuery(id+"F17.wireOp",EDGE,"E112.MirrorCS");Q34=makeQuery(id+"F17.imprint","IMPRINT",FACE,{"disambiguationData":[TD([[makeQuery(id+"F17.imprint","IMPRINT",EDGE,{"derivedFrom":subQ0}),-1.0]])]});}
            var Q35;
            {var subQ1=sQuery(id+"F17.wireOp",EDGE,"E103.MirrorCS");Q35=makeQuery(id+"F17.imprint","IMPRINT",FACE,{"disambiguationData":[TD([[makeQuery(id+"F17.imprint","IMPRINT",EDGE,{"derivedFrom":subQ1}),-1.0]])]});}
            var Q36;
            {var subQ0=sQuery(id+"F17.wireOp",EDGE,"E101.MirrorCS");var subQ1=sQuery(id+"F17.wireOp",EDGE,"E48");var subQ2=makeQuery(id+"F17.imprint","INTERSECT",VERTEX,{"derivedFrom":[subQ1,subQ0]});Q36=makeQuery(id+"F17.imprint","IMPRINT",FACE,{"disambiguationData":[TD([[makeQuery(id+"F17.imprint","IMPRINT",EDGE,{"disambiguationData":[TD([[subQ2,-1.0]])],"derivedFrom":subQ1}),1.0]])]});}
            var Q37;
            {var subQ0=sQuery(id+"F17.wireOp",EDGE,"E98.MirrorCS");var subQ1=sQuery(id+"F17.wireOp",EDGE,"E48");var subQ2=makeQuery(id+"F17.imprint","INTERSECT",VERTEX,{"derivedFrom":[subQ1,subQ0]});Q37=makeQuery(id+"F17.imprint","IMPRINT",FACE,{"disambiguationData":[TD([[makeQuery(id+"F17.imprint","IMPRINT",EDGE,{"disambiguationData":[TD([[subQ2,1.0]])],"derivedFrom":subQ1}),1.0]])]});}
            var Q38;
            {var subQ0=sQuery(id+"F17.wireOp",EDGE,"E100.MirrorCS");var subQ1=sQuery(id+"F17.wireOp",EDGE,"E48");var subQ2=makeQuery(id+"F17.imprint","INTERSECT",VERTEX,{"derivedFrom":[subQ1,subQ0]});Q38=makeQuery(id+"F17.imprint","IMPRINT",FACE,{"disambiguationData":[TD([[makeQuery(id+"F17.imprint","IMPRINT",EDGE,{"disambiguationData":[TD([[subQ2,-1.0]])],"derivedFrom":subQ1}),1.0]])]});}
            var Q39;
            {var subQ5=sQuery(id+"F17.wireOp",EDGE,"E105.MirrorCS");Q39=makeQuery(id+"F17.imprint","IMPRINT",FACE,{"disambiguationData":[TD([[makeQuery(id+"F17.imprint","IMPRINT",EDGE,{"derivedFrom":subQ5}),-1.0]])]});}
            var Q40;
            {var subQ0=sQuery(id+"F17.wireOp",EDGE,"E48");var subQ1=sQuery(id+"F17.wireOp",EDGE,"E39.2");var subQ2=makeQuery(id+"F17.imprint","INTERSECT",VERTEX,{"derivedFrom":[subQ1,subQ0]});Q40=makeQuery(id+"F17.imprint","IMPRINT",FACE,{"disambiguationData":[TD([[makeQuery(id+"F17.imprint","IMPRINT",EDGE,{"disambiguationData":[TD([[subQ2,1.0]])],"derivedFrom":subQ1}),-1.0]])]});}
            var Q41;
            {var subQ0=sQuery(id+"F17.wireOp",EDGE,"E120.MirrorCS");var subQ1=sQuery(id+"F17.wireOp",EDGE,"E98.MirrorCS");var subQ2=makeQuery(id+"F17.imprint","INTERSECT",VERTEX,{"derivedFrom":[subQ1,subQ0]});Q41=makeQuery(id+"F17.imprint","IMPRINT",FACE,{"disambiguationData":[TD([[makeQuery(id+"F17.imprint","IMPRINT",EDGE,{"disambiguationData":[TD([[subQ2,-1.0]])],"derivedFrom":subQ1}),1.0]])]});}
            var Q42;
            {var subQ0=sQuery(id+"F17.wireOp",EDGE,"E120.MirrorCS");var subQ1=sQuery(id+"F17.wireOp",EDGE,"E100.MirrorCS");var subQ2=makeQuery(id+"F17.imprint","INTERSECT",VERTEX,{"derivedFrom":[subQ1,subQ0]});Q42=makeQuery(id+"F17.imprint","IMPRINT",FACE,{"disambiguationData":[TD([[makeQuery(id+"F17.imprint","IMPRINT",EDGE,{"disambiguationData":[TD([[subQ2,-1.0]])],"derivedFrom":subQ1}),1.0]])]});}
            var Q43;
            Q43=makeQuery(id+"F17.imprint","IMPRINT",FACE,{"disambiguationData":[TD([[makeQuery(id+"F17.imprint","IMPRINT",EDGE,{"derivedFrom":sQuery(id+"F17.wireOp",EDGE,"E121.MirrorCS")}),1.0]])]});
            var Q44;
            {var subQ0=sQuery(id+"F17.wireOp",EDGE,"E120.MirrorCS");var subQ1=sQuery(id+"F17.wireOp",EDGE,"E98.MirrorCS");var subQ2=makeQuery(id+"F17.imprint","INTERSECT",VERTEX,{"derivedFrom":[subQ1,subQ0]});Q44=makeQuery(id+"F17.imprint","IMPRINT",FACE,{"disambiguationData":[TD([[makeQuery(id+"F17.imprint","IMPRINT",EDGE,{"disambiguationData":[TD([[subQ2,-1.0]])],"derivedFrom":subQ1}),-1.0]])]});}
            var Q45;
            {var subQ0=sQuery(id+"F17.wireOp",EDGE,"E120.MirrorCS");var subQ1=sQuery(id+"F17.wireOp",EDGE,"E99.MirrorCS");var subQ2=makeQuery(id+"F17.imprint","INTERSECT",VERTEX,{"derivedFrom":[subQ1,subQ0]});Q45=makeQuery(id+"F17.imprint","IMPRINT",FACE,{"disambiguationData":[TD([[makeQuery(id+"F17.imprint","IMPRINT",EDGE,{"disambiguationData":[TD([[subQ2,-1.0]])],"derivedFrom":subQ1}),-1.0]])]});}
            var Q46;
            {var subQ0=sQuery(id+"F17.wireOp",EDGE,"E120.MirrorCS");var subQ1=sQuery(id+"F17.wireOp",EDGE,"E101.MirrorCS");var subQ2=makeQuery(id+"F17.imprint","INTERSECT",VERTEX,{"derivedFrom":[subQ1,subQ0]});Q46=makeQuery(id+"F17.imprint","IMPRINT",FACE,{"disambiguationData":[TD([[makeQuery(id+"F17.imprint","IMPRINT",EDGE,{"disambiguationData":[TD([[subQ2,-1.0]])],"derivedFrom":subQ1}),1.0]])]});}
            var Q47;
            {var subQ6=sQuery(id+"F17.wireOp",EDGE,"E127.MirrorCS");Q47=makeQuery(id+"F17.imprint","IMPRINT",FACE,{"disambiguationData":[TD([[makeQuery(id+"F17.imprint","IMPRINT",EDGE,{"derivedFrom":subQ6}),-1.0]])]});}
            var Q48;
            {var subQ8=sQuery(id+"F17.wireOp",EDGE,"E122.MirrorCS");var subQ10=sQuery(id+"F17.wireOp",EDGE,"E160.MirrorCS");var subQ21=makeQuery(id+"F17.imprint","INTERSECT",VERTEX,{"derivedFrom":[subQ8,subQ10]});Q48=makeQuery(id+"F17.imprint","IMPRINT",FACE,{"disambiguationData":[TD([[makeQuery(id+"F17.imprint","IMPRINT",EDGE,{"disambiguationData":[TD([[subQ21,-1.0]])],"derivedFrom":subQ8}),-1.0]])]});}
            var Q49;
            {var subQ0=sQuery(id+"F17.wireOp",EDGE,"E142.MirrorCS");Q49=makeQuery(id+"F17.imprint","IMPRINT",FACE,{"disambiguationData":[TD([[makeQuery(id+"F17.imprint","IMPRINT",EDGE,{"derivedFrom":subQ0}),-1.0]])]});}
            var Q50;
            {var subQ0=sQuery(id+"F17.wireOp",EDGE,"E141.MirrorCS");Q50=makeQuery(id+"F17.imprint","IMPRINT",FACE,{"disambiguationData":[TD([[makeQuery(id+"F17.imprint","IMPRINT",EDGE,{"derivedFrom":subQ0}),-1.0]])]});}
            var Q51;
            {var subQ0=sQuery(id+"F17.wireOp",EDGE,"E140.MirrorCS");Q51=makeQuery(id+"F17.imprint","IMPRINT",FACE,{"disambiguationData":[TD([[makeQuery(id+"F17.imprint","IMPRINT",EDGE,{"derivedFrom":subQ0}),1.0]])]});}
            var Q52;
            {var subQ0=sQuery(id+"F17.wireOp",EDGE,"E137.MirrorCS");Q52=makeQuery(id+"F17.imprint","IMPRINT",FACE,{"disambiguationData":[TD([[makeQuery(id+"F17.imprint","IMPRINT",EDGE,{"derivedFrom":subQ0}),-1.0]])]});}
            var Q53;
            {var subQ0=sQuery(id+"F17.wireOp",EDGE,"E128.MirrorCS");Q53=makeQuery(id+"F17.imprint","IMPRINT",FACE,{"disambiguationData":[TD([[makeQuery(id+"F17.imprint","IMPRINT",EDGE,{"derivedFrom":subQ0}),-1.0]])]});}
            var Q54;
            {var subQ3=sQuery(id+"F17.wireOp",EDGE,"E131.MirrorCS");Q54=makeQuery(id+"F17.imprint","IMPRINT",FACE,{"disambiguationData":[TD([[makeQuery(id+"F17.imprint","IMPRINT",EDGE,{"derivedFrom":subQ3}),1.0]])]});}
            var Q55;
            {var subQ0=sQuery(id+"F17.wireOp",EDGE,"E133.MirrorCS");Q55=makeQuery(id+"F17.imprint","IMPRINT",FACE,{"disambiguationData":[TD([[makeQuery(id+"F17.imprint","IMPRINT",EDGE,{"derivedFrom":subQ0}),-1.0]])]});}
            var Q56;
            {var subQ0=sQuery(id+"F17.wireOp",EDGE,"E145.MirrorCS");Q56=makeQuery(id+"F17.imprint","IMPRINT",FACE,{"disambiguationData":[TD([[makeQuery(id+"F17.imprint","IMPRINT",EDGE,{"derivedFrom":subQ0}),-1.0]])]});}
            var Q57;
            {var subQ0=sQuery(id+"F17.wireOp",EDGE,"E134.MirrorCS");var subQ1=sQuery(id+"F17.wireOp",EDGE,"E39.2");var subQ2=makeQuery(id+"F17.imprint","INTERSECT",VERTEX,{"derivedFrom":[subQ1,subQ0]});Q57=makeQuery(id+"F17.imprint","IMPRINT",FACE,{"disambiguationData":[TD([[makeQuery(id+"F17.imprint","IMPRINT",EDGE,{"disambiguationData":[TD([[subQ2,-1.0]])],"derivedFrom":subQ1}),-1.0]])]});}
            var Q58;
            {var subQ3=sQuery(id+"F17.wireOp",EDGE,"E123.MirrorCS");var subQ5=sQuery(id+"F17.wireOp",EDGE,"E39.2");var subQ6=makeQuery(id+"F17.imprint","INTERSECT",VERTEX,{"derivedFrom":[subQ5,subQ3]});Q58=makeQuery(id+"F17.imprint","IMPRINT",FACE,{"disambiguationData":[TD([[makeQuery(id+"F17.imprint","IMPRINT",EDGE,{"disambiguationData":[TD([[subQ6,-1.0]])],"derivedFrom":subQ5}),-1.0]])]});}
            extrude(context, id + "F19", {"entities" : qUnion([Q0, Q1, Q2, Q3, Q4, Q5, Q6, Q7, Q8, Q9, Q10, Q11, Q12, Q13, Q14, Q15, Q16, Q17, Q18, Q19, Q20, Q21, Q22, Q23, Q24, Q25, Q26, Q27, Q28, Q29, Q30, Q31, Q32, Q33, Q34, Q35, Q36, Q37, Q38, Q39, Q40, Q41, Q42, Q43, Q44, Q45, Q46, Q47, Q48, Q49, Q50, Q51, Q52, Q53, Q54, Q55, Q56, Q57, Q58]), "operationType" : NewBodyOperationType.ADD, "oppositeDirection" : true, "depth" : 2 * mm, "offsetDistance" : 25 * mm});
        }
        {
            var Q0;
            Q0=makeQuery(id+"F8.boolean.opBoolean","COPY",FACE,{"derivedFrom":makeQuery(id+"F8.opExtrude","SWEPT_FACE",FACE,{"disambiguationData":[OSD([sQuery(id+"F7.wireOp",EDGE,"E14")])]})});
            var sketch = newSketch(context, id + "F20", { "sketchPlane" : qUnion([Q0])});
            skArc(sketch, "E163.0", {"start": v(-135, -157.5) * mm, "mid": v(0, -180.97) * mm, "end": v(135, -157.5) * mm});
            skLineSegment(sketch, "E164", {"start": v(-135, -157.5) * mm, "end": v(-135, -137.5) * mm});
            skLineSegment(sketch, "E165", {"start": v(-135, -137.5) * mm, "end": v(135, -137.5) * mm});
            skLineSegment(sketch, "E166", {"start": v(135, -137.5) * mm, "end": v(135, -157.5) * mm});
            skSolve(sketch);
        }
        {
            var Q0;
            Q0 = qSketchRegion(id + "F20", true);
            var Q1;
            Q1=makeQuery(id+"F8.boolean.opBoolean","COPY",FACE,{"derivedFrom":makeQuery(id+"F8.opExtrude","SWEPT_FACE",FACE,{"disambiguationData":[OSD([sQuery(id+"F7.wireOp",EDGE,"E13")])]})});
            extrude(context, id + "F21", {"entities" : qUnion([Q0]), "endBound" : BoundingType.UP_TO_SURFACE, "depth" : 25 * mm, "endBoundEntityFace" : qUnion([Q1]), "offsetDistance" : 25 * mm});
        }
        {
            var Q0;
            Q0=makeQuery(id+"F6.boolean.opBoolean","COPY",FACE,{"derivedFrom":makeQuery(id+"F6.opExtrude","CAP_FACE",FACE,{"disambiguationData":[OSD([sQuery(id+"F5.wireOp",EDGE,"E7.0.2"),sQuery(id+"F5.wireOp",EDGE,"E8"),sQuery(id+"F5.wireOp",EDGE,"E9"),sQuery(id+"F5.wireOp",EDGE,"E10.MirrorCS"),sQuery(id+"F5.wireOp",EDGE,"E11.MirrorCS")])],"isStart":true})});
            cPlane(context, id + "F22", {"entities" : qUnion([Q0]), "cplaneType" : CPlaneType.OFFSET, "offset" : 230 * mm, "width" : 150 * mm, "height" : 150 * mm});
        }
        {
            var Q0;
            Q0=qCreatedBy(id+"F22.planeOp",FACE);
            var sketch = newSketch(context, id + "F23", { "sketchPlane" : qUnion([Q0])});
            skLineSegment(sketch, "E167", {"start": v(0, 33.17) * mm, "end": v(0, -218.1) * mm, "construction": true});
            skLineSegment(sketch, "E168", {"start": v(-50, 0) * mm, "end": v(-50, -209.98) * mm, "construction": true});
            skLineSegment(sketch, "E169.0.0", {"start": v(-90, -129.3) * mm, "end": v(90, -129.3) * mm});
            skLineSegment(sketch, "E169.0.2", {"start": v(90, -129.3) * mm, "end": v(-90, -129.3) * mm});
            skLineSegment(sketch, "E170", {"start": v(-60, -129.3) * mm, "end": v(-56, -163.8) * mm});
            skLineSegment(sketch, "E171", {"start": v(-60.9, -163.8) * mm, "end": v(-38.9, -163.8) * mm});
            skLineSegment(sketch, "E172", {"start": v(-50, -163.8) * mm, "end": v(-50, -129.3) * mm});
            skSolve(sketch);
        }
        {
            var Q0;
            {var subQ0=sQuery(id+"F23.wireOp",EDGE,"E170");Q0=makeQuery(id+"F23.imprint","IMPRINT",FACE,{"disambiguationData":[TD([[makeQuery(id+"F23.imprint","IMPRINT",EDGE,{"derivedFrom":subQ0}),1.0]])]});}
            var Q1;
            Q1=sQuery(id+"F23.wireOp",EDGE,"E172");
            revolve(context, id + "F24", {"surfaceOperationType" : NewSurfaceOperationType.NEW, "entities" : qUnion([Q0]), "axis" : qUnion([Q1]), "revolveType" : RevolveType.FULL});
        }
        {
            var Q0;
            Q0=makeQuery(id+"F24.opRevolve","SWEPT_FACE",FACE,{"disambiguationData":[OSD([sQuery(id+"F23.wireOp",EDGE,"E171")])]});
            var sketch = newSketch(context, id + "F25", { "sketchPlane" : qUnion([Q0])});
            skCircle(sketch, "E173.0", {"center": v(-50, 680) * mm, "radius": 6 * mm, "construction": true});
            skLineSegment(sketch, "E174", {"start": v(-50, 717.97) * mm, "end": v(-50, 638.06) * mm, "construction": true});
            skLineSegment(sketch, "E175.bottom", {"start": v(-60, 695) * mm, "end": v(-40, 695) * mm});
            skLineSegment(sketch, "E175.top", {"start": v(-57, 665) * mm, "end": v(-57, 665) * mm});
            skLineSegment(sketch, "E175.left", {"start": v(-60, 695) * mm, "end": v(-60, 668) * mm});
            skLineSegment(sketch, "E176.top", {"start": v(-54, 655) * mm, "end": v(-46, 655) * mm});
            skLineSegment(sketch, "E176.left", {"start": v(-54, 662) * mm, "end": v(-54, 655) * mm});
            skPoint(sketch, "E177.visualSharp", {"position": v(-60, 665) * mm});
            skArc(sketch, "E177.filletArc", {"start": v(-60, 668) * mm, "mid": v(-59.12, 665.88) * mm, "end": v(-57, 665) * mm});
            skArc(sketch, "E178.filletArc", {"start": v(-54, 662) * mm, "mid": v(-54.88, 664.12) * mm, "end": v(-57, 665) * mm});
            skLineSegment(sketch, "E179", {"start": v(-57, 665) * mm, "end": v(-50, 665) * mm});
            skLineSegment(sketch, "E180", {"start": v(-50, 695) * mm, "end": v(-50, 655) * mm});
            skSolve(sketch);
        }
        {
            var Q0;
            {var subQ1=sQuery(id+"F25.wireOp",EDGE,"E175.left");Q0=makeQuery(id+"F25.imprint","IMPRINT",FACE,{"disambiguationData":[TD([[makeQuery(id+"F25.imprint","IMPRINT",EDGE,{"derivedFrom":subQ1}),1.0]])]});}
            var Q1;
            {var subQ0=sQuery(id+"F25.wireOp",EDGE,"E180");var subQ1=makeQuery(id+"F24.opRevolve","SWEPT_EDGE",EDGE,{"disambiguationData":[OSD([sQuery(id+"F23.wireOp",EDGE,"E170"),sQuery(id+"F23.wireOp",EDGE,"E171")])]});var subQ2=makeQuery(id+"F25.imprint","INTERSECT",VERTEX,{"disambiguationData":[OD(0.0)],"derivedFrom":[subQ1,subQ0]});Q1=makeQuery(id+"F25.imprint","IMPRINT",FACE,{"disambiguationData":[TD([[makeQuery(id+"F25.imprint","IMPRINT",EDGE,{"disambiguationData":[TD([[subQ2,-1.0]])],"derivedFrom":subQ0}),-1.0]])]});}
            var Q2;
            {var subQ1=sQuery(id+"F25.wireOp",EDGE,"E176.left");Q2=makeQuery(id+"F25.imprint","IMPRINT",FACE,{"disambiguationData":[TD([[makeQuery(id+"F25.imprint","IMPRINT",EDGE,{"derivedFrom":subQ1}),1.0]])]});}
            var Q3;
            Q3=sQuery(id+"F25.wireOp",EDGE,"E174");
            revolve(context, id + "F26", {"operationType" : NewBodyOperationType.ADD, "surfaceOperationType" : NewSurfaceOperationType.NEW, "entities" : qUnion([Q0, Q1, Q2]), "axis" : qUnion([Q3]), "revolveType" : RevolveType.FULL});
        }
        {
            var Q0;
            Q0=sQuery(id+"F25.wireOp",VERTEX,"E175.left.start");
            var Q1;
            Q1=sQuery(id+"F25.wireOp",VERTEX,"E177.filletArc.start");
            var Q2;
            Q2=sQuery(id+"F25.wireOp",VERTEX,"E173.0.center");
            cPlane(context, id + "F27", {"entities" : qUnion([Q0, Q1, Q2]), "cplaneType" : CPlaneType.THREE_POINT, "offset" : 25 * mm, "width" : 150 * mm, "height" : 150 * mm});
        }
        {
            var Q0;
            Q0=qCreatedBy(id+"F27.planeOp",FACE);
            var sketch = newSketch(context, id + "F28", { "sketchPlane" : qUnion([Q0])});
            skLineSegment(sketch, "E181.0", {"start": v(40, 695) * mm, "end": v(60, 695) * mm});
            skLineSegment(sketch, "E182", {"start": v(50, 714.18) * mm, "end": v(50, 675.84) * mm, "construction": true});
            skPoint(sketch, "E182.startSnap0", {"position": v(50, 695) * mm});
            skLineSegment(sketch, "E183", {"start": v(48, 695) * mm, "end": v(48, 700) * mm});
            skLineSegment(sketch, "E184", {"start": v(48, 700) * mm, "end": v(42.5, 700) * mm});
            skLineSegment(sketch, "E185", {"start": v(42.5, 700) * mm, "end": v(42.5, 715) * mm});
            skLineSegment(sketch, "E186", {"start": v(42.5, 715) * mm, "end": v(57.5, 715) * mm});
            skLineSegment(sketch, "E187", {"start": v(57.5, 715) * mm, "end": v(57.5, 700) * mm});
            skLineSegment(sketch, "E188", {"start": v(57.5, 700) * mm, "end": v(52, 700) * mm});
            skLineSegment(sketch, "E189", {"start": v(52, 700) * mm, "end": v(52, 695) * mm});
            skLineSegment(sketch, "E190.bottom", {"start": v(44.5, 713) * mm, "end": v(55.5, 713) * mm});
            skLineSegment(sketch, "E190.top", {"start": v(44.5, 702) * mm, "end": v(55.5, 702) * mm});
            skLineSegment(sketch, "E190.left", {"start": v(44.5, 713) * mm, "end": v(44.5, 702) * mm});
            skLineSegment(sketch, "E190.right", {"start": v(55.5, 713) * mm, "end": v(55.5, 702) * mm});
            skSolve(sketch);
        }
        {
            var Q0;
            {var subQ1=sQuery(id+"F28.wireOp",EDGE,"E183");Q0=makeQuery(id+"F28.imprint","IMPRINT",FACE,{"disambiguationData":[TD([[makeQuery(id+"F28.imprint","IMPRINT",EDGE,{"derivedFrom":subQ1}),-1.0]])]});}
            extrude(context, id + "F29", {"entities" : qUnion([Q0]), "operationType" : NewBodyOperationType.ADD, "endBound" : BoundingType.SYMMETRIC, "depth" : 5 * mm, "offsetDistance" : 25 * mm});
        }
        {
            var Q0;
            Q0=makeQuery(id+"F29.opExtrude","SWEPT_EDGE",EDGE,{"disambiguationData":[OSD([sQuery(id+"F28.wireOp",EDGE,"E186"),sQuery(id+"F28.wireOp",EDGE,"E187")])]});
            var Q1;
            Q1=makeQuery(id+"F29.opExtrude","SWEPT_EDGE",EDGE,{"disambiguationData":[OSD([sQuery(id+"F28.wireOp",EDGE,"E187"),sQuery(id+"F28.wireOp",EDGE,"E188")])]});
            var Q2;
            Q2=makeQuery(id+"F29.opExtrude","SWEPT_EDGE",EDGE,{"disambiguationData":[OSD([sQuery(id+"F28.wireOp",EDGE,"E185"),sQuery(id+"F28.wireOp",EDGE,"E186")])]});
            var Q3;
            Q3=makeQuery(id+"F29.opExtrude","SWEPT_EDGE",EDGE,{"disambiguationData":[OSD([sQuery(id+"F28.wireOp",EDGE,"E184"),sQuery(id+"F28.wireOp",EDGE,"E185")])]});
            fillet(context, id + "F30", {"entities" : qUnion([Q0, Q1, Q2, Q3]), "radius" : 3 * mm, "tangentPropagation" : true, "allowEdgeOverflow" : false});
        }
        {
            var Q0;
            Q0=makeQuery(id+"F29.opExtrude","SWEPT_EDGE",EDGE,{"disambiguationData":[OSD([sQuery(id+"F28.wireOp",EDGE,"E190.bottom"),sQuery(id+"F28.wireOp",EDGE,"E190.right")])]});
            var Q1;
            Q1=makeQuery(id+"F29.opExtrude","SWEPT_EDGE",EDGE,{"disambiguationData":[OSD([sQuery(id+"F28.wireOp",EDGE,"E190.bottom"),sQuery(id+"F28.wireOp",EDGE,"E190.left")])]});
            var Q2;
            Q2=makeQuery(id+"F29.opExtrude","SWEPT_EDGE",EDGE,{"disambiguationData":[OSD([sQuery(id+"F28.wireOp",EDGE,"E190.top"),sQuery(id+"F28.wireOp",EDGE,"E190.left")])]});
            var Q3;
            Q3=makeQuery(id+"F29.opExtrude","SWEPT_EDGE",EDGE,{"disambiguationData":[OSD([sQuery(id+"F28.wireOp",EDGE,"E190.top"),sQuery(id+"F28.wireOp",EDGE,"E190.right")])]});
            fillet(context, id + "F31", {"entities" : qUnion([Q0, Q1, Q2, Q3]), "radius" : 1 * mm, "tangentPropagation" : true, "allowEdgeOverflow" : false});
        }
        {
            var Q0;
            Q0=makeQuery(id+"F24.opRevolve","SWEPT_BODY",BODY,{"disambiguationData":[OSD([sQuery(id+"F23.wireOp",EDGE,"E169.0.2"),sQuery(id+"F23.wireOp",EDGE,"E170"),sQuery(id+"F23.wireOp",EDGE,"E171"),sQuery(id+"F23.wireOp",EDGE,"E172")])]});
            var Q1;
            Q1=qCreatedBy(makeId("Right.planeOp"),FACE);
            mirror(context, id + "F32", {"entities" : qUnion([Q0]), "mirrorPlane" : qUnion([Q1])});
        }
        {
            var Q0;
            Q0=qCreatedBy(makeId("Right.planeOp"),FACE);
            cPlane(context, id + "F33", {"entities" : qUnion([Q0]), "cplaneType" : CPlaneType.OFFSET, "offset" : (315 / 2 - 50) * mm, "width" : 150 * mm, "height" : 150 * mm});
        }
        {
            var Q0;
            Q0=qCreatedBy(id+"F33.planeOp",FACE);
            var sketch = newSketch(context, id + "F34", { "sketchPlane" : qUnion([Q0])});
            skLineSegment(sketch, "E191", {"start": v(157.5, 920) * mm, "end": v(166.5, 920) * mm});
            skLineSegment(sketch, "E192", {"start": v(166.5, 920) * mm, "end": v(157.5, 904.41) * mm});
            skLineSegment(sketch, "E193", {"start": v(157.5, 904.41) * mm, "end": v(157.5, 886.41) * mm});
            skLineSegment(sketch, "E194", {"start": v(157.5, 886.41) * mm, "end": v(149.5, 886.41) * mm});
            skLineSegment(sketch, "E195", {"start": v(149.5, 886.41) * mm, "end": v(149.5, 920) * mm});
            skLineSegment(sketch, "E196", {"start": v(149.5, 920) * mm, "end": v(157.5, 920) * mm});
            skSolve(sketch);
        }
        {
            var Q0;
            Q0 = qSketchRegion(id + "F34", true);
            extrude(context, id + "F35", {"entities" : qUnion([Q0]), "operationType" : NewBodyOperationType.REMOVE, "endBound" : BoundingType.SYMMETRIC, "oppositeDirection" : true, "depth" : 10 * mm, "offsetDistance" : 25 * mm});
        }
        {
            var Q0;
            Q0=qCreatedBy(id+"F33.planeOp",FACE);
            cPlane(context, id + "F36", {"entities" : qUnion([Q0]), "cplaneType" : CPlaneType.OFFSET, "offset" : 20 * mm, "oppositeDirection" : true, "width" : 150 * mm, "height" : 150 * mm});
        }
        {
            var Q0;
            Q0=qCreatedBy(id+"F36.planeOp",FACE);
            var sketch = newSketch(context, id + "F37", { "sketchPlane" : qUnion([Q0])});
            skLineSegment(sketch, "E197.0", {"start": v(157.5, 886.41) * mm, "end": v(149.5, 886.41) * mm});
            skLineSegment(sketch, "E197.1", {"start": v(149.5, 886.41) * mm, "end": v(149.5, 920) * mm});
            skLineSegment(sketch, "E197.2", {"start": v(149.5, 920) * mm, "end": v(157.5, 920) * mm});
            skLineSegment(sketch, "E197.3", {"start": v(157.5, 920) * mm, "end": v(166.5, 920) * mm});
            skLineSegment(sketch, "E197.4", {"start": v(166.5, 920) * mm, "end": v(157.5, 904.41) * mm});
            skLineSegment(sketch, "E197.5", {"start": v(157.5, 904.41) * mm, "end": v(157.5, 886.41) * mm});
            skSolve(sketch);
        }
        {
            var Q0;
            Q0 = qSketchRegion(id + "F37", true);
            extrude(context, id + "F38", {"entities" : qUnion([Q0]), "operationType" : NewBodyOperationType.REMOVE, "endBound" : BoundingType.SYMMETRIC, "oppositeDirection" : true, "depth" : 10 * mm, "offsetDistance" : 25 * mm});
        }
        {
            var Q0;
            Q0 = qSketchRegion(id + "F34", true);
            extrude(context, id + "F39", {"entities" : qUnion([Q0]), "endBound" : BoundingType.SYMMETRIC, "depth" : 10 * mm, "offsetDistance" : 25 * mm});
        }
        {
            var Q0;
            Q0 = qSketchRegion(id + "F37", true);
            extrude(context, id + "F40", {"entities" : qUnion([Q0]), "endBound" : BoundingType.SYMMETRIC, "depth" : 10 * mm, "offsetDistance" : 25 * mm});
        }
        {
            var Q0;
            {var subQ0=sQuery(id+"F0.wireOp",EDGE,"E0.left");var subQ1=sQuery(id+"F0.wireOp",EDGE,"E0.bottom");Q0=makeQuery(id+"F13.opFillet","BLEND_VERTEX",VERTEX,{"blendedFrom":[makeQuery(id+"F1.opExtrude","CAP_VERTEX",VERTEX,{"disambiguationData":[OSD([subQ1,subQ0])],"isStart":false}),makeQuery(id+"F1.opExtrude","SWEPT_EDGE",EDGE,{"disambiguationData":[OSD([subQ1,subQ0])]}),makeQuery(id+"F1.opExtrude","CAP_EDGE",EDGE,{"disambiguationData":[OSD([subQ0])],"isStart":false}),makeQuery(id+"F1.opExtrude","SWEPT_FACE",FACE,{"disambiguationData":[OSD([subQ0])]})],"blendedInto":[makeQuery(id+"F1.opExtrude","SWEPT_FACE",FACE,{"disambiguationData":[OSD([subQ0])]})]});}
            var Q1;
            {var subQ0=sQuery(id+"F0.wireOp",EDGE,"E1");var subQ1=sQuery(id+"F0.wireOp",EDGE,"E0.top");var subQ2=sQuery(id+"F0.wireOp",EDGE,"E0.left");var subQ3=makeQuery(id+"F1.opExtrude","SWEPT_FACE",FACE,{"disambiguationData":[OSD([subQ2])]});var subQ4=sQuery(id+"F0.wireOp",EDGE,"E0.bottom");Q1=makeQuery(id+"F13.opFillet","BLEND_VERTEX",VERTEX,{"blendedFrom":[makeQuery(id+"F1.opExtrude","SWEPT_EDGE",EDGE,{"disambiguationData":[OSD([subQ4,subQ2])]}),subQ3,makeQuery(id+"F10.boolean.opBoolean","SPLIT",FACE,{"disambiguationData":[TD([subQ3])],"derivedFrom":makeQuery(id+"F1.opExtrude","CAP_FACE",FACE,{"disambiguationData":[OSD([subQ4,subQ1,subQ2,sQuery(id+"F0.wireOp",EDGE,"E0.right"),subQ0])],"isStart":true})})],"blendedInto":[subQ3,makeQuery(id+"F10.boolean.opBoolean","SPLIT",FACE,{"disambiguationData":[TD([subQ3])],"derivedFrom":makeQuery(id+"F1.opExtrude","CAP_FACE",FACE,{"disambiguationData":[OSD([subQ4,subQ1,subQ2,sQuery(id+"F0.wireOp",EDGE,"E0.right"),subQ0])],"isStart":true})})]});}
            var Q2;
            {var subQ0=sQuery(id+"F0.wireOp",EDGE,"E0.right");var subQ1=sQuery(id+"F0.wireOp",EDGE,"E0.bottom");Q2=makeQuery(id+"F13.opFillet","BLEND_VERTEX",VERTEX,{"blendedFrom":[makeQuery(id+"F1.opExtrude","CAP_VERTEX",VERTEX,{"disambiguationData":[OSD([subQ1,subQ0])],"isStart":false}),makeQuery(id+"F1.opExtrude","SWEPT_EDGE",EDGE,{"disambiguationData":[OSD([subQ1,subQ0])]}),makeQuery(id+"F1.opExtrude","CAP_EDGE",EDGE,{"disambiguationData":[OSD([subQ0])],"isStart":false}),makeQuery(id+"F1.opExtrude","SWEPT_FACE",FACE,{"disambiguationData":[OSD([subQ0])]})],"blendedInto":[makeQuery(id+"F1.opExtrude","SWEPT_FACE",FACE,{"disambiguationData":[OSD([subQ0])]})]});}
            cPlane(context, id + "F41", {"entities" : qUnion([Q0, Q1, Q2]), "cplaneType" : CPlaneType.THREE_POINT, "offset" : 25 * mm, "width" : 150 * mm, "height" : 150 * mm});
        }
        {
            var Q0;
            Q0=qCreatedBy(id+"F41.planeOp",FACE);
            var sketch = newSketch(context, id + "F42", { "sketchPlane" : qUnion([Q0])});
            skLineSegment(sketch, "E198.bottom", {"start": v(-125, 945) * mm, "end": v(125, 945) * mm});
            skLineSegment(sketch, "E198.top", {"start": v(-125, 855) * mm, "end": v(125, 855) * mm});
            skLineSegment(sketch, "E198.left", {"start": v(-125, 945) * mm, "end": v(-125, 855) * mm});
            skLineSegment(sketch, "E198.right", {"start": v(125, 945) * mm, "end": v(125, 855) * mm});
            skSolve(sketch);
        }
        {
            var Q0;
            Q0 = qSketchRegion(id + "F42", true);
            extrude(context, id + "F43", {"entities" : qUnion([Q0]), "operationType" : NewBodyOperationType.REMOVE, "endBound" : BoundingType.THROUGH_ALL, "depth" : 25 * mm, "offsetDistance" : 25 * mm});
        }
        {
            var Q0;
            Q0=makeQuery(id+"F43.boolean.opBoolean","COPY",FACE,{"derivedFrom":makeQuery(id+"F43.opExtrude","CAP_FACE",FACE,{"disambiguationData":[OSD([sQuery(id+"F42.wireOp",EDGE,"E198.bottom"),sQuery(id+"F42.wireOp",EDGE,"E198.top"),sQuery(id+"F42.wireOp",EDGE,"E198.left"),sQuery(id+"F42.wireOp",EDGE,"E198.right")])],"isStart":true})});
            var sketch = newSketch(context, id + "F44", { "sketchPlane" : qUnion([Q0])});
            skLineSegment(sketch, "E199.bottom", {"start": v(-125, 945) * mm, "end": v(125, 945) * mm});
            skLineSegment(sketch, "E199.top", {"start": v(-125, 855) * mm, "end": v(125, 855) * mm});
            skLineSegment(sketch, "E199.left", {"start": v(-125, 945) * mm, "end": v(-125, 855) * mm});
            skLineSegment(sketch, "E199.right", {"start": v(125, 945) * mm, "end": v(125, 855) * mm});
            skLineSegment(sketch, "E200.bottom", {"start": v(75, 930) * mm, "end": v(85, 930) * mm});
            skLineSegment(sketch, "E200.top", {"start": v(75, 925) * mm, "end": v(85, 925) * mm});
            skLineSegment(sketch, "E200.left", {"start": v(75, 930) * mm, "end": v(75, 925) * mm});
            skLineSegment(sketch, "E200.right", {"start": v(85, 930) * mm, "end": v(85, 925) * mm});
            skLineSegment(sketch, "E201.bottom", {"start": v(75, 920) * mm, "end": v(85, 920) * mm});
            skLineSegment(sketch, "E201.top", {"start": v(75, 915) * mm, "end": v(85, 915) * mm});
            skLineSegment(sketch, "E201.left", {"start": v(75, 920) * mm, "end": v(75, 915) * mm});
            skLineSegment(sketch, "E201.right", {"start": v(85, 920) * mm, "end": v(85, 915) * mm});
            skSolve(sketch);
        }
        {
            var Q0;
            Q0=makeQuery(id+"F44.imprint","IMPRINT",FACE,{"disambiguationData":[TD([[makeQuery(id+"F44.imprint","IMPRINT",EDGE,{"derivedFrom":sQuery(id+"F44.wireOp",EDGE,"E199.bottom")}),-1.0]])]});
            var Q1;
            Q1=makeQuery(id+"F44.imprint","IMPRINT",FACE,{"disambiguationData":[TD([[makeQuery(id+"F44.imprint","IMPRINT",EDGE,{"derivedFrom":sQuery(id+"F44.wireOp",EDGE,"6fba481b-f54a-40dc-850f-529da61e2d5d.sketch_text.stroke-14")}),1.0]])]});
            var Q2;
            Q2=makeQuery(id+"F44.imprint","IMPRINT",FACE,{"disambiguationData":[TD([[makeQuery(id+"F44.imprint","IMPRINT",EDGE,{"derivedFrom":sQuery(id+"F44.wireOp",EDGE,"6fba481b-f54a-40dc-850f-529da61e2d5d.sketch_text.stroke-50")}),1.0]])]});
            var Q3;
            Q3=makeQuery(id+"F44.imprint","IMPRINT",FACE,{"disambiguationData":[TD([[makeQuery(id+"F44.imprint","IMPRINT",EDGE,{"derivedFrom":sQuery(id+"F44.wireOp",EDGE,"0e071c30-8112-48db-a0b7-94a150164aee.sketch_text.stroke-20")}),1.0]])]});
            var Q4;
            Q4=makeQuery(id+"F44.imprint","IMPRINT",FACE,{"disambiguationData":[TD([[makeQuery(id+"F44.imprint","IMPRINT",EDGE,{"derivedFrom":sQuery(id+"F44.wireOp",EDGE,"e2d7af9a-f6d1-4b82-89d6-a8a0b8d7c55a.sketch_text.stroke-23")}),1.0]])]});
            var Q5;
            Q5=makeQuery(id+"F44.imprint","IMPRINT",FACE,{"disambiguationData":[TD([[makeQuery(id+"F44.imprint","IMPRINT",EDGE,{"derivedFrom":sQuery(id+"F44.wireOp",EDGE,"e2d7af9a-f6d1-4b82-89d6-a8a0b8d7c55a.sketch_text.stroke-44")}),1.0]])]});
            var Q6;
            {var subQ0=sQuery(id+"F0.wireOp",EDGE,"E0.right");var subQ1=sQuery(id+"F0.wireOp",EDGE,"E0.bottom");var subQ2=sQuery(id+"F0.wireOp",EDGE,"E1");var subQ4=sQuery(id+"F0.wireOp",EDGE,"E0.left");Q6=makeQuery(id+"F6.boolean.opBoolean","SPLIT",FACE,{"disambiguationData":[TD([makeQuery(id+"F1.opExtrude","CAP_FACE",FACE,{"disambiguationData":[OSD([subQ1,sQuery(id+"F0.wireOp",EDGE,"E0.top"),subQ4,subQ0,subQ2])],"isStart":false})])],"derivedFrom":makeQuery(id+"F1.opExtrude","SWEPT_FACE",FACE,{"disambiguationData":[OSD([subQ2])]})});}
            extrude(context, id + "F45", {"entities" : qUnion([Q0, Q1, Q2, Q3, Q4, Q5]), "operationType" : NewBodyOperationType.ADD, "endBound" : BoundingType.UP_TO_SURFACE, "depth" : 25 * mm, "endBoundEntityFace" : qUnion([Q6]), "offsetDistance" : 25 * mm});
        }
        {
            var Q0;
            Q0=makeQuery(id+"F44.imprint","IMPRINT",FACE,{"disambiguationData":[TD([[makeQuery(id+"F44.imprint","IMPRINT",EDGE,{"derivedFrom":sQuery(id+"F44.wireOp",EDGE,"E200.bottom")}),-1.0]])]});
            var Q1;
            {var subQ0=sQuery(id+"F0.wireOp",EDGE,"E0.right");var subQ1=sQuery(id+"F0.wireOp",EDGE,"E0.bottom");var subQ2=sQuery(id+"F0.wireOp",EDGE,"E1");var subQ4=sQuery(id+"F0.wireOp",EDGE,"E0.left");Q1=makeQuery(id+"F45.boolean.opBoolean","MERGE",FACE,{"derivedFrom":[makeQuery(id+"F6.boolean.opBoolean","SPLIT",FACE,{"disambiguationData":[TD([makeQuery(id+"F1.opExtrude","CAP_FACE",FACE,{"disambiguationData":[OSD([subQ1,sQuery(id+"F0.wireOp",EDGE,"E0.top"),subQ4,subQ0,subQ2])],"isStart":false})])],"derivedFrom":makeQuery(id+"F1.opExtrude","SWEPT_FACE",FACE,{"disambiguationData":[OSD([subQ2])]})}),makeQuery(id+"F45.opExtrude","CAP_FACE",FACE,{"disambiguationData":[OSD([sQuery(id+"F44.wireOp",EDGE,"E199.bottom"),sQuery(id+"F44.wireOp",EDGE,"E199.top"),sQuery(id+"F44.wireOp",EDGE,"E199.left"),sQuery(id+"F44.wireOp",EDGE,"E199.right"),sQuery(id+"F44.wireOp",EDGE,"E200.bottom"),sQuery(id+"F44.wireOp",EDGE,"E200.top"),sQuery(id+"F44.wireOp",EDGE,"E200.left"),sQuery(id+"F44.wireOp",EDGE,"E200.right"),sQuery(id+"F44.wireOp",EDGE,"E201.bottom"),sQuery(id+"F44.wireOp",EDGE,"E201.top"),sQuery(id+"F44.wireOp",EDGE,"E201.left"),sQuery(id+"F44.wireOp",EDGE,"E201.right"),sQuery(id+"F44.wireOp",EDGE,"0e071c30-8112-48db-a0b7-94a150164aee.sketch_text.stroke-0"),sQuery(id+"F44.wireOp",EDGE,"0e071c30-8112-48db-a0b7-94a150164aee.sketch_text.stroke-1"),sQuery(id+"F44.wireOp",EDGE,"0e071c30-8112-48db-a0b7-94a150164aee.sketch_text.stroke-2"),sQuery(id+"F44.wireOp",EDGE,"0e071c30-8112-48db-a0b7-94a150164aee.sketch_text.stroke-3"),sQuery(id+"F44.wireOp",EDGE,"0e071c30-8112-48db-a0b7-94a150164aee.sketch_text.stroke-4"),sQuery(id+"F44.wireOp",EDGE,"0e071c30-8112-48db-a0b7-94a150164aee.sketch_text.stroke-5"),sQuery(id+"F44.wireOp",EDGE,"0e071c30-8112-48db-a0b7-94a150164aee.sketch_text.stroke-6"),sQuery(id+"F44.wireOp",EDGE,"0e071c30-8112-48db-a0b7-94a150164aee.sketch_text.stroke-7"),sQuery(id+"F44.wireOp",EDGE,"0e071c30-8112-48db-a0b7-94a150164aee.sketch_text.stroke-8"),sQuery(id+"F44.wireOp",EDGE,"0e071c30-8112-48db-a0b7-94a150164aee.sketch_text.stroke-9"),sQuery(id+"F44.wireOp",EDGE,"0e071c30-8112-48db-a0b7-94a150164aee.sketch_text.stroke-10"),sQuery(id+"F44.wireOp",EDGE,"0e071c30-8112-48db-a0b7-94a150164aee.sketch_text.stroke-11"),sQuery(id+"F44.wireOp",EDGE,"0e071c30-8112-48db-a0b7-94a150164aee.sketch_text.stroke-12"),sQuery(id+"F44.wireOp",EDGE,"0e071c30-8112-48db-a0b7-94a150164aee.sketch_text.stroke-13"),sQuery(id+"F44.wireOp",EDGE,"0e071c30-8112-48db-a0b7-94a150164aee.sketch_text.stroke-14"),sQuery(id+"F44.wireOp",EDGE,"0e071c30-8112-48db-a0b7-94a150164aee.sketch_text.stroke-15"),sQuery(id+"F44.wireOp",EDGE,"0e071c30-8112-48db-a0b7-94a150164aee.sketch_text.stroke-16"),sQuery(id+"F44.wireOp",EDGE,"0e071c30-8112-48db-a0b7-94a150164aee.sketch_text.stroke-17"),sQuery(id+"F44.wireOp",EDGE,"0e071c30-8112-48db-a0b7-94a150164aee.sketch_text.stroke-18"),sQuery(id+"F44.wireOp",EDGE,"0e071c30-8112-48db-a0b7-94a150164aee.sketch_text.stroke-19"),sQuery(id+"F44.wireOp",EDGE,"0e071c30-8112-48db-a0b7-94a150164aee.sketch_text.stroke-28"),sQuery(id+"F44.wireOp",EDGE,"0e071c30-8112-48db-a0b7-94a150164aee.sketch_text.stroke-29"),sQuery(id+"F44.wireOp",EDGE,"0e071c30-8112-48db-a0b7-94a150164aee.sketch_text.stroke-30"),sQuery(id+"F44.wireOp",EDGE,"0e071c30-8112-48db-a0b7-94a150164aee.sketch_text.stroke-31"),sQuery(id+"F44.wireOp",EDGE,"0e071c30-8112-48db-a0b7-94a150164aee.sketch_text.stroke-32"),sQuery(id+"F44.wireOp",EDGE,"0e071c30-8112-48db-a0b7-94a150164aee.sketch_text.stroke-33"),sQuery(id+"F44.wireOp",EDGE,"0e071c30-8112-48db-a0b7-94a150164aee.sketch_text.stroke-34"),sQuery(id+"F44.wireOp",EDGE,"0e071c30-8112-48db-a0b7-94a150164aee.sketch_text.stroke-35"),sQuery(id+"F44.wireOp",EDGE,"e2d7af9a-f6d1-4b82-89d6-a8a0b8d7c55a.sketch_text.stroke-0"),sQuery(id+"F44.wireOp",EDGE,"e2d7af9a-f6d1-4b82-89d6-a8a0b8d7c55a.sketch_text.stroke-1"),sQuery(id+"F44.wireOp",EDGE,"e2d7af9a-f6d1-4b82-89d6-a8a0b8d7c55a.sketch_text.stroke-2"),sQuery(id+"F44.wireOp",EDGE,"e2d7af9a-f6d1-4b82-89d6-a8a0b8d7c55a.sketch_text.stroke-3"),sQuery(id+"F44.wireOp",EDGE,"e2d7af9a-f6d1-4b82-89d6-a8a0b8d7c55a.sketch_text.stroke-4"),sQuery(id+"F44.wireOp",EDGE,"e2d7af9a-f6d1-4b82-89d6-a8a0b8d7c55a.sketch_text.stroke-5"),sQuery(id+"F44.wireOp",EDGE,"e2d7af9a-f6d1-4b82-89d6-a8a0b8d7c55a.sketch_text.stroke-6"),sQuery(id+"F44.wireOp",EDGE,"e2d7af9a-f6d1-4b82-89d6-a8a0b8d7c55a.sketch_text.stroke-7"),sQuery(id+"F44.wireOp",EDGE,"e2d7af9a-f6d1-4b82-89d6-a8a0b8d7c55a.sketch_text.stroke-8"),sQuery(id+"F44.wireOp",EDGE,"e2d7af9a-f6d1-4b82-89d6-a8a0b8d7c55a.sketch_text.stroke-9"),sQuery(id+"F44.wireOp",EDGE,"e2d7af9a-f6d1-4b82-89d6-a8a0b8d7c55a.sketch_text.stroke-10"),sQuery(id+"F44.wireOp",EDGE,"e2d7af9a-f6d1-4b82-89d6-a8a0b8d7c55a.sketch_text.stroke-11"),sQuery(id+"F44.wireOp",EDGE,"e2d7af9a-f6d1-4b82-89d6-a8a0b8d7c55a.sketch_text.stroke-12"),sQuery(id+"F44.wireOp",EDGE,"e2d7af9a-f6d1-4b82-89d6-a8a0b8d7c55a.sketch_text.stroke-13"),sQuery(id+"F44.wireOp",EDGE,"e2d7af9a-f6d1-4b82-89d6-a8a0b8d7c55a.sketch_text.stroke-14"),sQuery(id+"F44.wireOp",EDGE,"e2d7af9a-f6d1-4b82-89d6-a8a0b8d7c55a.sketch_text.stroke-15"),sQuery(id+"F44.wireOp",EDGE,"e2d7af9a-f6d1-4b82-89d6-a8a0b8d7c55a.sketch_text.stroke-16"),sQuery(id+"F44.wireOp",EDGE,"e2d7af9a-f6d1-4b82-89d6-a8a0b8d7c55a.sketch_text.stroke-17"),sQuery(id+"F44.wireOp",EDGE,"e2d7af9a-f6d1-4b82-89d6-a8a0b8d7c55a.sketch_text.stroke-18"),sQuery(id+"F44.wireOp",EDGE,"e2d7af9a-f6d1-4b82-89d6-a8a0b8d7c55a.sketch_text.stroke-19"),sQuery(id+"F44.wireOp",EDGE,"e2d7af9a-f6d1-4b82-89d6-a8a0b8d7c55a.sketch_text.stroke-20"),sQuery(id+"F44.wireOp",EDGE,"e2d7af9a-f6d1-4b82-89d6-a8a0b8d7c55a.sketch_text.stroke-21"),sQuery(id+"F44.wireOp",EDGE,"e2d7af9a-f6d1-4b82-89d6-a8a0b8d7c55a.sketch_text.stroke-22"),sQuery(id+"F44.wireOp",EDGE,"e2d7af9a-f6d1-4b82-89d6-a8a0b8d7c55a.sketch_text.stroke-31"),sQuery(id+"F44.wireOp",EDGE,"e2d7af9a-f6d1-4b82-89d6-a8a0b8d7c55a.sketch_text.stroke-32"),sQuery(id+"F44.wireOp",EDGE,"e2d7af9a-f6d1-4b82-89d6-a8a0b8d7c55a.sketch_text.stroke-33"),sQuery(id+"F44.wireOp",EDGE,"e2d7af9a-f6d1-4b82-89d6-a8a0b8d7c55a.sketch_text.stroke-34"),sQuery(id+"F44.wireOp",EDGE,"e2d7af9a-f6d1-4b82-89d6-a8a0b8d7c55a.sketch_text.stroke-35"),sQuery(id+"F44.wireOp",EDGE,"e2d7af9a-f6d1-4b82-89d6-a8a0b8d7c55a.sketch_text.stroke-36"),sQuery(id+"F44.wireOp",EDGE,"e2d7af9a-f6d1-4b82-89d6-a8a0b8d7c55a.sketch_text.stroke-37"),sQuery(id+"F44.wireOp",EDGE,"e2d7af9a-f6d1-4b82-89d6-a8a0b8d7c55a.sketch_text.stroke-38"),sQuery(id+"F44.wireOp",EDGE,"e2d7af9a-f6d1-4b82-89d6-a8a0b8d7c55a.sketch_text.stroke-39"),sQuery(id+"F44.wireOp",EDGE,"e2d7af9a-f6d1-4b82-89d6-a8a0b8d7c55a.sketch_text.stroke-40"),sQuery(id+"F44.wireOp",EDGE,"e2d7af9a-f6d1-4b82-89d6-a8a0b8d7c55a.sketch_text.stroke-41"),sQuery(id+"F44.wireOp",EDGE,"e2d7af9a-f6d1-4b82-89d6-a8a0b8d7c55a.sketch_text.stroke-42"),sQuery(id+"F44.wireOp",EDGE,"e2d7af9a-f6d1-4b82-89d6-a8a0b8d7c55a.sketch_text.stroke-43"),sQuery(id+"F44.wireOp",EDGE,"6fba481b-f54a-40dc-850f-529da61e2d5d.sketch_text.stroke-0"),sQuery(id+"F44.wireOp",EDGE,"6fba481b-f54a-40dc-850f-529da61e2d5d.sketch_text.stroke-1"),sQuery(id+"F44.wireOp",EDGE,"6fba481b-f54a-40dc-850f-529da61e2d5d.sketch_text.stroke-2"),sQuery(id+"F44.wireOp",EDGE,"6fba481b-f54a-40dc-850f-529da61e2d5d.sketch_text.stroke-3"),sQuery(id+"F44.wireOp",EDGE,"6fba481b-f54a-40dc-850f-529da61e2d5d.sketch_text.stroke-4"),sQuery(id+"F44.wireOp",EDGE,"6fba481b-f54a-40dc-850f-529da61e2d5d.sketch_text.stroke-5"),sQuery(id+"F44.wireOp",EDGE,"6fba481b-f54a-40dc-850f-529da61e2d5d.sketch_text.stroke-6"),sQuery(id+"F44.wireOp",EDGE,"6fba481b-f54a-40dc-850f-529da61e2d5d.sketch_text.stroke-7"),sQuery(id+"F44.wireOp",EDGE,"6fba481b-f54a-40dc-850f-529da61e2d5d.sketch_text.stroke-8"),sQuery(id+"F44.wireOp",EDGE,"6fba481b-f54a-40dc-850f-529da61e2d5d.sketch_text.stroke-9"),sQuery(id+"F44.wireOp",EDGE,"6fba481b-f54a-40dc-850f-529da61e2d5d.sketch_text.stroke-10"),sQuery(id+"F44.wireOp",EDGE,"6fba481b-f54a-40dc-850f-529da61e2d5d.sketch_text.stroke-11"),sQuery(id+"F44.wireOp",EDGE,"6fba481b-f54a-40dc-850f-529da61e2d5d.sketch_text.stroke-12"),sQuery(id+"F44.wireOp",EDGE,"6fba481b-f54a-40dc-850f-529da61e2d5d.sketch_text.stroke-13"),sQuery(id+"F44.wireOp",EDGE,"6fba481b-f54a-40dc-850f-529da61e2d5d.sketch_text.stroke-22"),sQuery(id+"F44.wireOp",EDGE,"6fba481b-f54a-40dc-850f-529da61e2d5d.sketch_text.stroke-23"),sQuery(id+"F44.wireOp",EDGE,"6fba481b-f54a-40dc-850f-529da61e2d5d.sketch_text.stroke-24"),sQuery(id+"F44.wireOp",EDGE,"6fba481b-f54a-40dc-850f-529da61e2d5d.sketch_text.stroke-25"),sQuery(id+"F44.wireOp",EDGE,"6fba481b-f54a-40dc-850f-529da61e2d5d.sketch_text.stroke-26"),sQuery(id+"F44.wireOp",EDGE,"6fba481b-f54a-40dc-850f-529da61e2d5d.sketch_text.stroke-27"),sQuery(id+"F44.wireOp",EDGE,"6fba481b-f54a-40dc-850f-529da61e2d5d.sketch_text.stroke-28"),sQuery(id+"F44.wireOp",EDGE,"6fba481b-f54a-40dc-850f-529da61e2d5d.sketch_text.stroke-29"),sQuery(id+"F44.wireOp",EDGE,"6fba481b-f54a-40dc-850f-529da61e2d5d.sketch_text.stroke-30"),sQuery(id+"F44.wireOp",EDGE,"6fba481b-f54a-40dc-850f-529da61e2d5d.sketch_text.stroke-31"),sQuery(id+"F44.wireOp",EDGE,"6fba481b-f54a-40dc-850f-529da61e2d5d.sketch_text.stroke-32"),sQuery(id+"F44.wireOp",EDGE,"6fba481b-f54a-40dc-850f-529da61e2d5d.sketch_text.stroke-33"),sQuery(id+"F44.wireOp",EDGE,"6fba481b-f54a-40dc-850f-529da61e2d5d.sketch_text.stroke-34"),sQuery(id+"F44.wireOp",EDGE,"6fba481b-f54a-40dc-850f-529da61e2d5d.sketch_text.stroke-35"),sQuery(id+"F44.wireOp",EDGE,"6fba481b-f54a-40dc-850f-529da61e2d5d.sketch_text.stroke-36"),sQuery(id+"F44.wireOp",EDGE,"6fba481b-f54a-40dc-850f-529da61e2d5d.sketch_text.stroke-37"),sQuery(id+"F44.wireOp",EDGE,"6fba481b-f54a-40dc-850f-529da61e2d5d.sketch_text.stroke-38"),sQuery(id+"F44.wireOp",EDGE,"6fba481b-f54a-40dc-850f-529da61e2d5d.sketch_text.stroke-39"),sQuery(id+"F44.wireOp",EDGE,"6fba481b-f54a-40dc-850f-529da61e2d5d.sketch_text.stroke-40"),sQuery(id+"F44.wireOp",EDGE,"6fba481b-f54a-40dc-850f-529da61e2d5d.sketch_text.stroke-41"),sQuery(id+"F44.wireOp",EDGE,"6fba481b-f54a-40dc-850f-529da61e2d5d.sketch_text.stroke-42"),sQuery(id+"F44.wireOp",EDGE,"6fba481b-f54a-40dc-850f-529da61e2d5d.sketch_text.stroke-43"),sQuery(id+"F44.wireOp",EDGE,"6fba481b-f54a-40dc-850f-529da61e2d5d.sketch_text.stroke-44"),sQuery(id+"F44.wireOp",EDGE,"6fba481b-f54a-40dc-850f-529da61e2d5d.sketch_text.stroke-45"),sQuery(id+"F44.wireOp",EDGE,"6fba481b-f54a-40dc-850f-529da61e2d5d.sketch_text.stroke-46"),sQuery(id+"F44.wireOp",EDGE,"6fba481b-f54a-40dc-850f-529da61e2d5d.sketch_text.stroke-47"),sQuery(id+"F44.wireOp",EDGE,"6fba481b-f54a-40dc-850f-529da61e2d5d.sketch_text.stroke-48"),sQuery(id+"F44.wireOp",EDGE,"6fba481b-f54a-40dc-850f-529da61e2d5d.sketch_text.stroke-49")])],"isStart":false})]});}
            extrude(context, id + "F46", {"entities" : qUnion([Q0]), "endBound" : BoundingType.UP_TO_SURFACE, "depth" : 25 * mm, "endBoundEntityFace" : qUnion([Q1]), "offsetDistance" : 25 * mm});
        }
        {
            var Q0;
            Q0=makeQuery(id+"F44.imprint","IMPRINT",FACE,{"disambiguationData":[TD([[makeQuery(id+"F44.imprint","IMPRINT",EDGE,{"derivedFrom":sQuery(id+"F44.wireOp",EDGE,"E201.bottom")}),-1.0]])]});
            var Q1;
            {var subQ0=sQuery(id+"F0.wireOp",EDGE,"E0.right");var subQ1=sQuery(id+"F0.wireOp",EDGE,"E0.bottom");var subQ2=sQuery(id+"F0.wireOp",EDGE,"E1");var subQ4=sQuery(id+"F0.wireOp",EDGE,"E0.left");Q1=makeQuery(id+"F45.boolean.opBoolean","MERGE",FACE,{"derivedFrom":[makeQuery(id+"F6.boolean.opBoolean","SPLIT",FACE,{"disambiguationData":[TD([makeQuery(id+"F1.opExtrude","CAP_FACE",FACE,{"disambiguationData":[OSD([subQ1,sQuery(id+"F0.wireOp",EDGE,"E0.top"),subQ4,subQ0,subQ2])],"isStart":false})])],"derivedFrom":makeQuery(id+"F1.opExtrude","SWEPT_FACE",FACE,{"disambiguationData":[OSD([subQ2])]})}),makeQuery(id+"F45.opExtrude","CAP_FACE",FACE,{"disambiguationData":[OSD([sQuery(id+"F44.wireOp",EDGE,"E199.bottom"),sQuery(id+"F44.wireOp",EDGE,"E199.top"),sQuery(id+"F44.wireOp",EDGE,"E199.left"),sQuery(id+"F44.wireOp",EDGE,"E199.right"),sQuery(id+"F44.wireOp",EDGE,"E200.bottom"),sQuery(id+"F44.wireOp",EDGE,"E200.top"),sQuery(id+"F44.wireOp",EDGE,"E200.left"),sQuery(id+"F44.wireOp",EDGE,"E200.right"),sQuery(id+"F44.wireOp",EDGE,"E201.bottom"),sQuery(id+"F44.wireOp",EDGE,"E201.top"),sQuery(id+"F44.wireOp",EDGE,"E201.left"),sQuery(id+"F44.wireOp",EDGE,"E201.right"),sQuery(id+"F44.wireOp",EDGE,"0e071c30-8112-48db-a0b7-94a150164aee.sketch_text.stroke-0"),sQuery(id+"F44.wireOp",EDGE,"0e071c30-8112-48db-a0b7-94a150164aee.sketch_text.stroke-1"),sQuery(id+"F44.wireOp",EDGE,"0e071c30-8112-48db-a0b7-94a150164aee.sketch_text.stroke-2"),sQuery(id+"F44.wireOp",EDGE,"0e071c30-8112-48db-a0b7-94a150164aee.sketch_text.stroke-3"),sQuery(id+"F44.wireOp",EDGE,"0e071c30-8112-48db-a0b7-94a150164aee.sketch_text.stroke-4"),sQuery(id+"F44.wireOp",EDGE,"0e071c30-8112-48db-a0b7-94a150164aee.sketch_text.stroke-5"),sQuery(id+"F44.wireOp",EDGE,"0e071c30-8112-48db-a0b7-94a150164aee.sketch_text.stroke-6"),sQuery(id+"F44.wireOp",EDGE,"0e071c30-8112-48db-a0b7-94a150164aee.sketch_text.stroke-7"),sQuery(id+"F44.wireOp",EDGE,"0e071c30-8112-48db-a0b7-94a150164aee.sketch_text.stroke-8"),sQuery(id+"F44.wireOp",EDGE,"0e071c30-8112-48db-a0b7-94a150164aee.sketch_text.stroke-9"),sQuery(id+"F44.wireOp",EDGE,"0e071c30-8112-48db-a0b7-94a150164aee.sketch_text.stroke-10"),sQuery(id+"F44.wireOp",EDGE,"0e071c30-8112-48db-a0b7-94a150164aee.sketch_text.stroke-11"),sQuery(id+"F44.wireOp",EDGE,"0e071c30-8112-48db-a0b7-94a150164aee.sketch_text.stroke-12"),sQuery(id+"F44.wireOp",EDGE,"0e071c30-8112-48db-a0b7-94a150164aee.sketch_text.stroke-13"),sQuery(id+"F44.wireOp",EDGE,"0e071c30-8112-48db-a0b7-94a150164aee.sketch_text.stroke-14"),sQuery(id+"F44.wireOp",EDGE,"0e071c30-8112-48db-a0b7-94a150164aee.sketch_text.stroke-15"),sQuery(id+"F44.wireOp",EDGE,"0e071c30-8112-48db-a0b7-94a150164aee.sketch_text.stroke-16"),sQuery(id+"F44.wireOp",EDGE,"0e071c30-8112-48db-a0b7-94a150164aee.sketch_text.stroke-17"),sQuery(id+"F44.wireOp",EDGE,"0e071c30-8112-48db-a0b7-94a150164aee.sketch_text.stroke-18"),sQuery(id+"F44.wireOp",EDGE,"0e071c30-8112-48db-a0b7-94a150164aee.sketch_text.stroke-19"),sQuery(id+"F44.wireOp",EDGE,"0e071c30-8112-48db-a0b7-94a150164aee.sketch_text.stroke-28"),sQuery(id+"F44.wireOp",EDGE,"0e071c30-8112-48db-a0b7-94a150164aee.sketch_text.stroke-29"),sQuery(id+"F44.wireOp",EDGE,"0e071c30-8112-48db-a0b7-94a150164aee.sketch_text.stroke-30"),sQuery(id+"F44.wireOp",EDGE,"0e071c30-8112-48db-a0b7-94a150164aee.sketch_text.stroke-31"),sQuery(id+"F44.wireOp",EDGE,"0e071c30-8112-48db-a0b7-94a150164aee.sketch_text.stroke-32"),sQuery(id+"F44.wireOp",EDGE,"0e071c30-8112-48db-a0b7-94a150164aee.sketch_text.stroke-33"),sQuery(id+"F44.wireOp",EDGE,"0e071c30-8112-48db-a0b7-94a150164aee.sketch_text.stroke-34"),sQuery(id+"F44.wireOp",EDGE,"0e071c30-8112-48db-a0b7-94a150164aee.sketch_text.stroke-35"),sQuery(id+"F44.wireOp",EDGE,"e2d7af9a-f6d1-4b82-89d6-a8a0b8d7c55a.sketch_text.stroke-0"),sQuery(id+"F44.wireOp",EDGE,"e2d7af9a-f6d1-4b82-89d6-a8a0b8d7c55a.sketch_text.stroke-1"),sQuery(id+"F44.wireOp",EDGE,"e2d7af9a-f6d1-4b82-89d6-a8a0b8d7c55a.sketch_text.stroke-2"),sQuery(id+"F44.wireOp",EDGE,"e2d7af9a-f6d1-4b82-89d6-a8a0b8d7c55a.sketch_text.stroke-3"),sQuery(id+"F44.wireOp",EDGE,"e2d7af9a-f6d1-4b82-89d6-a8a0b8d7c55a.sketch_text.stroke-4"),sQuery(id+"F44.wireOp",EDGE,"e2d7af9a-f6d1-4b82-89d6-a8a0b8d7c55a.sketch_text.stroke-5"),sQuery(id+"F44.wireOp",EDGE,"e2d7af9a-f6d1-4b82-89d6-a8a0b8d7c55a.sketch_text.stroke-6"),sQuery(id+"F44.wireOp",EDGE,"e2d7af9a-f6d1-4b82-89d6-a8a0b8d7c55a.sketch_text.stroke-7"),sQuery(id+"F44.wireOp",EDGE,"e2d7af9a-f6d1-4b82-89d6-a8a0b8d7c55a.sketch_text.stroke-8"),sQuery(id+"F44.wireOp",EDGE,"e2d7af9a-f6d1-4b82-89d6-a8a0b8d7c55a.sketch_text.stroke-9"),sQuery(id+"F44.wireOp",EDGE,"e2d7af9a-f6d1-4b82-89d6-a8a0b8d7c55a.sketch_text.stroke-10"),sQuery(id+"F44.wireOp",EDGE,"e2d7af9a-f6d1-4b82-89d6-a8a0b8d7c55a.sketch_text.stroke-11"),sQuery(id+"F44.wireOp",EDGE,"e2d7af9a-f6d1-4b82-89d6-a8a0b8d7c55a.sketch_text.stroke-12"),sQuery(id+"F44.wireOp",EDGE,"e2d7af9a-f6d1-4b82-89d6-a8a0b8d7c55a.sketch_text.stroke-13"),sQuery(id+"F44.wireOp",EDGE,"e2d7af9a-f6d1-4b82-89d6-a8a0b8d7c55a.sketch_text.stroke-14"),sQuery(id+"F44.wireOp",EDGE,"e2d7af9a-f6d1-4b82-89d6-a8a0b8d7c55a.sketch_text.stroke-15"),sQuery(id+"F44.wireOp",EDGE,"e2d7af9a-f6d1-4b82-89d6-a8a0b8d7c55a.sketch_text.stroke-16"),sQuery(id+"F44.wireOp",EDGE,"e2d7af9a-f6d1-4b82-89d6-a8a0b8d7c55a.sketch_text.stroke-17"),sQuery(id+"F44.wireOp",EDGE,"e2d7af9a-f6d1-4b82-89d6-a8a0b8d7c55a.sketch_text.stroke-18"),sQuery(id+"F44.wireOp",EDGE,"e2d7af9a-f6d1-4b82-89d6-a8a0b8d7c55a.sketch_text.stroke-19"),sQuery(id+"F44.wireOp",EDGE,"e2d7af9a-f6d1-4b82-89d6-a8a0b8d7c55a.sketch_text.stroke-20"),sQuery(id+"F44.wireOp",EDGE,"e2d7af9a-f6d1-4b82-89d6-a8a0b8d7c55a.sketch_text.stroke-21"),sQuery(id+"F44.wireOp",EDGE,"e2d7af9a-f6d1-4b82-89d6-a8a0b8d7c55a.sketch_text.stroke-22"),sQuery(id+"F44.wireOp",EDGE,"e2d7af9a-f6d1-4b82-89d6-a8a0b8d7c55a.sketch_text.stroke-31"),sQuery(id+"F44.wireOp",EDGE,"e2d7af9a-f6d1-4b82-89d6-a8a0b8d7c55a.sketch_text.stroke-32"),sQuery(id+"F44.wireOp",EDGE,"e2d7af9a-f6d1-4b82-89d6-a8a0b8d7c55a.sketch_text.stroke-33"),sQuery(id+"F44.wireOp",EDGE,"e2d7af9a-f6d1-4b82-89d6-a8a0b8d7c55a.sketch_text.stroke-34"),sQuery(id+"F44.wireOp",EDGE,"e2d7af9a-f6d1-4b82-89d6-a8a0b8d7c55a.sketch_text.stroke-35"),sQuery(id+"F44.wireOp",EDGE,"e2d7af9a-f6d1-4b82-89d6-a8a0b8d7c55a.sketch_text.stroke-36"),sQuery(id+"F44.wireOp",EDGE,"e2d7af9a-f6d1-4b82-89d6-a8a0b8d7c55a.sketch_text.stroke-37"),sQuery(id+"F44.wireOp",EDGE,"e2d7af9a-f6d1-4b82-89d6-a8a0b8d7c55a.sketch_text.stroke-38"),sQuery(id+"F44.wireOp",EDGE,"e2d7af9a-f6d1-4b82-89d6-a8a0b8d7c55a.sketch_text.stroke-39"),sQuery(id+"F44.wireOp",EDGE,"e2d7af9a-f6d1-4b82-89d6-a8a0b8d7c55a.sketch_text.stroke-40"),sQuery(id+"F44.wireOp",EDGE,"e2d7af9a-f6d1-4b82-89d6-a8a0b8d7c55a.sketch_text.stroke-41"),sQuery(id+"F44.wireOp",EDGE,"e2d7af9a-f6d1-4b82-89d6-a8a0b8d7c55a.sketch_text.stroke-42"),sQuery(id+"F44.wireOp",EDGE,"e2d7af9a-f6d1-4b82-89d6-a8a0b8d7c55a.sketch_text.stroke-43"),sQuery(id+"F44.wireOp",EDGE,"6fba481b-f54a-40dc-850f-529da61e2d5d.sketch_text.stroke-0"),sQuery(id+"F44.wireOp",EDGE,"6fba481b-f54a-40dc-850f-529da61e2d5d.sketch_text.stroke-1"),sQuery(id+"F44.wireOp",EDGE,"6fba481b-f54a-40dc-850f-529da61e2d5d.sketch_text.stroke-2"),sQuery(id+"F44.wireOp",EDGE,"6fba481b-f54a-40dc-850f-529da61e2d5d.sketch_text.stroke-3"),sQuery(id+"F44.wireOp",EDGE,"6fba481b-f54a-40dc-850f-529da61e2d5d.sketch_text.stroke-4"),sQuery(id+"F44.wireOp",EDGE,"6fba481b-f54a-40dc-850f-529da61e2d5d.sketch_text.stroke-5"),sQuery(id+"F44.wireOp",EDGE,"6fba481b-f54a-40dc-850f-529da61e2d5d.sketch_text.stroke-6"),sQuery(id+"F44.wireOp",EDGE,"6fba481b-f54a-40dc-850f-529da61e2d5d.sketch_text.stroke-7"),sQuery(id+"F44.wireOp",EDGE,"6fba481b-f54a-40dc-850f-529da61e2d5d.sketch_text.stroke-8"),sQuery(id+"F44.wireOp",EDGE,"6fba481b-f54a-40dc-850f-529da61e2d5d.sketch_text.stroke-9"),sQuery(id+"F44.wireOp",EDGE,"6fba481b-f54a-40dc-850f-529da61e2d5d.sketch_text.stroke-10"),sQuery(id+"F44.wireOp",EDGE,"6fba481b-f54a-40dc-850f-529da61e2d5d.sketch_text.stroke-11"),sQuery(id+"F44.wireOp",EDGE,"6fba481b-f54a-40dc-850f-529da61e2d5d.sketch_text.stroke-12"),sQuery(id+"F44.wireOp",EDGE,"6fba481b-f54a-40dc-850f-529da61e2d5d.sketch_text.stroke-13"),sQuery(id+"F44.wireOp",EDGE,"6fba481b-f54a-40dc-850f-529da61e2d5d.sketch_text.stroke-22"),sQuery(id+"F44.wireOp",EDGE,"6fba481b-f54a-40dc-850f-529da61e2d5d.sketch_text.stroke-23"),sQuery(id+"F44.wireOp",EDGE,"6fba481b-f54a-40dc-850f-529da61e2d5d.sketch_text.stroke-24"),sQuery(id+"F44.wireOp",EDGE,"6fba481b-f54a-40dc-850f-529da61e2d5d.sketch_text.stroke-25"),sQuery(id+"F44.wireOp",EDGE,"6fba481b-f54a-40dc-850f-529da61e2d5d.sketch_text.stroke-26"),sQuery(id+"F44.wireOp",EDGE,"6fba481b-f54a-40dc-850f-529da61e2d5d.sketch_text.stroke-27"),sQuery(id+"F44.wireOp",EDGE,"6fba481b-f54a-40dc-850f-529da61e2d5d.sketch_text.stroke-28"),sQuery(id+"F44.wireOp",EDGE,"6fba481b-f54a-40dc-850f-529da61e2d5d.sketch_text.stroke-29"),sQuery(id+"F44.wireOp",EDGE,"6fba481b-f54a-40dc-850f-529da61e2d5d.sketch_text.stroke-30"),sQuery(id+"F44.wireOp",EDGE,"6fba481b-f54a-40dc-850f-529da61e2d5d.sketch_text.stroke-31"),sQuery(id+"F44.wireOp",EDGE,"6fba481b-f54a-40dc-850f-529da61e2d5d.sketch_text.stroke-32"),sQuery(id+"F44.wireOp",EDGE,"6fba481b-f54a-40dc-850f-529da61e2d5d.sketch_text.stroke-33"),sQuery(id+"F44.wireOp",EDGE,"6fba481b-f54a-40dc-850f-529da61e2d5d.sketch_text.stroke-34"),sQuery(id+"F44.wireOp",EDGE,"6fba481b-f54a-40dc-850f-529da61e2d5d.sketch_text.stroke-35"),sQuery(id+"F44.wireOp",EDGE,"6fba481b-f54a-40dc-850f-529da61e2d5d.sketch_text.stroke-36"),sQuery(id+"F44.wireOp",EDGE,"6fba481b-f54a-40dc-850f-529da61e2d5d.sketch_text.stroke-37"),sQuery(id+"F44.wireOp",EDGE,"6fba481b-f54a-40dc-850f-529da61e2d5d.sketch_text.stroke-38"),sQuery(id+"F44.wireOp",EDGE,"6fba481b-f54a-40dc-850f-529da61e2d5d.sketch_text.stroke-39"),sQuery(id+"F44.wireOp",EDGE,"6fba481b-f54a-40dc-850f-529da61e2d5d.sketch_text.stroke-40"),sQuery(id+"F44.wireOp",EDGE,"6fba481b-f54a-40dc-850f-529da61e2d5d.sketch_text.stroke-41"),sQuery(id+"F44.wireOp",EDGE,"6fba481b-f54a-40dc-850f-529da61e2d5d.sketch_text.stroke-42"),sQuery(id+"F44.wireOp",EDGE,"6fba481b-f54a-40dc-850f-529da61e2d5d.sketch_text.stroke-43"),sQuery(id+"F44.wireOp",EDGE,"6fba481b-f54a-40dc-850f-529da61e2d5d.sketch_text.stroke-44"),sQuery(id+"F44.wireOp",EDGE,"6fba481b-f54a-40dc-850f-529da61e2d5d.sketch_text.stroke-45"),sQuery(id+"F44.wireOp",EDGE,"6fba481b-f54a-40dc-850f-529da61e2d5d.sketch_text.stroke-46"),sQuery(id+"F44.wireOp",EDGE,"6fba481b-f54a-40dc-850f-529da61e2d5d.sketch_text.stroke-47"),sQuery(id+"F44.wireOp",EDGE,"6fba481b-f54a-40dc-850f-529da61e2d5d.sketch_text.stroke-48"),sQuery(id+"F44.wireOp",EDGE,"6fba481b-f54a-40dc-850f-529da61e2d5d.sketch_text.stroke-49")])],"isStart":false})]});}
            extrude(context, id + "F47", {"entities" : qUnion([Q0]), "endBound" : BoundingType.UP_TO_SURFACE, "depth" : 25 * mm, "endBoundEntityFace" : qUnion([Q1]), "offsetDistance" : 25 * mm});
        }
    });
